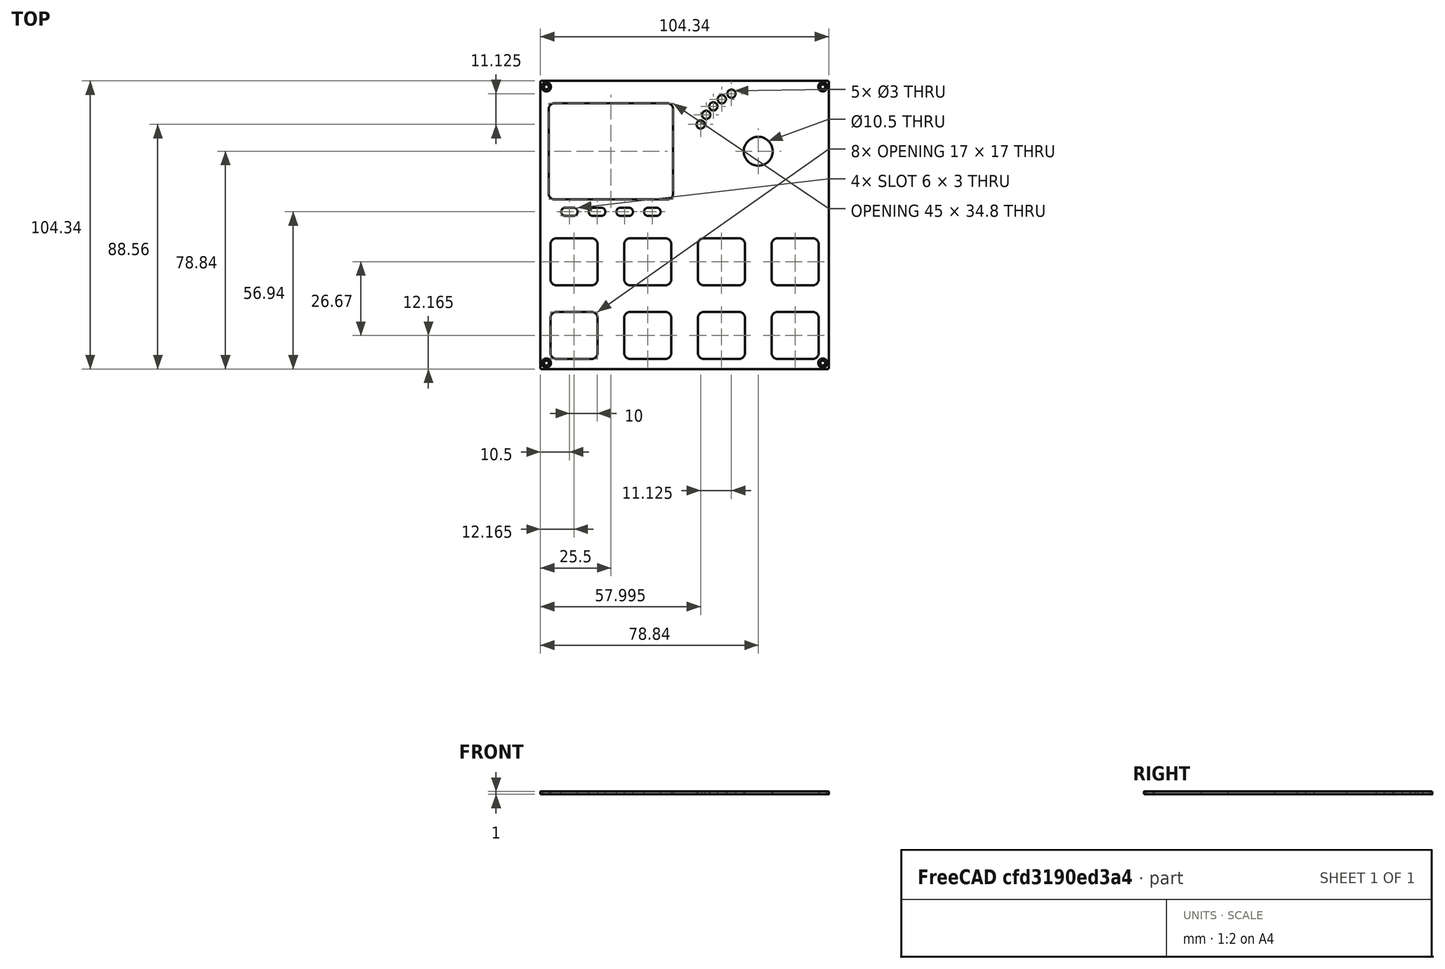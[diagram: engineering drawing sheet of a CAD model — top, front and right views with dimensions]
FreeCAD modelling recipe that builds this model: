
FCSTD DOCUMENT  (FreeCAD 0.21R33771 (Git))
Label: FRONTPANEL-SHEET-VSN1
License: All rights reserved
LicenseURL: https://en.wikipedia.org/wiki/All_rights_reserved
objects: TechDraw::DrawViewDimension×16, TechDraw::DrawViewBalloon×13, Sketcher::SketchObject×11, PartDesign::Pocket×5, TechDraw::DrawViewPart×5, TechDraw::DrawHatch×5, TechDraw::DrawViewAnnotation×4, PartDesign::Body×2, TechDraw::DrawSVGTemplate×2, TechDraw::DrawPage×2, Spreadsheet::Sheet×1, PartDesign::Pad×1, PartDesign::Hole×1, PartDesign::FeatureBase×1, TechDraw::DrawComplexSection×1
note: 54 computed .brp shape members not serialized (recipe doc carries the construction recipe); baked Part::Feature solids carry a one-line shape summary decoded from their .brp

FEATURE [Spreadsheet::Sheet] Spreadsheet  label="dim"
  cells = A1='panel_length; B1(panel_length)=104.35; A2='panel_thickness; B2(panel_thickness)=1; A3='panel_radius; B3(panel_radius)==(104.35 - 103.6) / 2; A5='corner_drill_dist; B5(corner_drill_dist)=100; A6='corner_drill_dia; B6(corner_drill_dia)=1.75; A7='corner_drill_countersink; B7(corner_drill_countersink)=3.3; A9='undercut_width; B9(undercut_width)=1; A10='undercut_length; B10(undercut_length)=90; A11='undercut_offset; B11(undercut_offset)=1; A12='undercut_depth; B12(undercut_depth)=0.8; A14='ui_raster; B14(ui_raster)=26.67; A16='light_drill_dia; B16(light_drill_dia)=3; D16='old 2.9; A17='light_bore_dia; B17(light_bore_dia)=3.45; C17='check; D17='old 3.30; E17='DEPRICATED; A18='light_bore_depth; B18(light_bore_depth)=0.4; C18='check; D18='old 0.40; E18='DEPRICATED; A20='pot_drill_dia; B20(pot_drill_dia)=9.8; C20='check; D20='old 6.20; A21='pot_led_dist; B21(pot_led_dist)=8.5; B22=0; A23='but_drill_dia; B23(but_drill_dia)=9.8; A24='but_led_dist; B24(but_led_dist)=8.5; A26='fad_cutout_width; B26(fad_cutout_width)=2.1; C26='check; D26='old 1.50; A27='fad_cutout_length; B27(fad_cutout_length)=36; A28='fad_led_dist; B28(fad_led_dist)=25; A30='enc_drill_dia; B30(enc_drill_dia)=9.8; C30='check; D30='old 6.20; A31='enc_led_dist; B31(enc_led_dist)=8.5; A33='longfad_cutout_width; B33(longfad_cutout_width)=2.1; A34='longfad_cutout_length; B34(longfad_cutout_length)=66; A36='panel_chamfer; B36(panel_chamfer)=0.2; C36='UPDATE DRAWING
FEATURE [Sketcher::SketchObject] Sketch025
  FullyConstrained = true
  MapMode = 5
  Support = -> [XY_Plane011]
  expr: Constraints[49] = <<dim>>.light_drill_dia
  sketch-geometry (28):
    g0: Circle CenterX=-26.67 CenterY=26.67 CenterZ=0 NormalX=0 NormalY=0 NormalZ=1 AngleXU=0 Radius=5.25
    g1: Circle CenterX=26.67 CenterY=26.67 CenterZ=0 NormalX=0 NormalY=0 NormalZ=1 AngleXU=0 Radius=5.25
    g2: LineSegment StartX=-26.67 StartY=26.67 StartZ=0 EndX=0 EndY=26.67 EndZ=0
    g3: LineSegment StartX=0 StartY=26.67 StartZ=0 EndX=0 EndY=0 EndZ=0
    g4: LineSegment StartX=26.67 StartY=26.67 StartZ=0 EndX=0 EndY=26.67 EndZ=0
    g5: Circle CenterX=-26.67 CenterY=26.67 CenterZ=0 NormalX=0 NormalY=0 NormalZ=1 AngleXU=0 Radius=23
    g6: Circle CenterX=26.67 CenterY=26.67 CenterZ=0 NormalX=0 NormalY=0 NormalZ=1 AngleXU=0 Radius=23
    g7: Circle CenterX=-47.5151 CenterY=36.3902 CenterZ=0 NormalX=0 NormalY=0 NormalZ=1 AngleXU=0 Radius=1.5
    g8: Circle CenterX=-45.5105 CenterY=39.8623 CenterZ=0 NormalX=0 NormalY=0 NormalZ=1 AngleXU=0 Radius=1.5
    g9: Circle CenterX=-42.9335 CenterY=42.9335 CenterZ=0 NormalX=0 NormalY=0 NormalZ=1 AngleXU=0 Radius=1.5
    g10: Circle CenterX=-39.8623 CenterY=45.5105 CenterZ=0 NormalX=0 NormalY=0 NormalZ=1 AngleXU=0 Radius=1.5
    g11: Circle CenterX=-36.3902 CenterY=47.5151 CenterZ=0 NormalX=0 NormalY=0 NormalZ=1 AngleXU=0 Radius=1.5
    g12: Circle CenterX=5.82492 CenterY=36.3902 CenterZ=0 NormalX=0 NormalY=0 NormalZ=1 AngleXU=0 Radius=1.5
    g13: Circle CenterX=7.8295 CenterY=39.8623 CenterZ=0 NormalX=0 NormalY=0 NormalZ=1 AngleXU=0 Radius=1.5
    g14: Circle CenterX=10.4065 CenterY=42.9335 CenterZ=0 NormalX=0 NormalY=0 NormalZ=1 AngleXU=0 Radius=1.5
    g15: Circle CenterX=13.4777 CenterY=45.5105 CenterZ=0 NormalX=0 NormalY=0 NormalZ=1 AngleXU=0 Radius=1.5
    g16: Circle CenterX=16.9498 CenterY=47.5151 CenterZ=0 NormalX=0 NormalY=0 NormalZ=1 AngleXU=0 Radius=1.5
    g17: LineSegment StartX=-47.5151 StartY=36.3902 StartZ=0 EndX=5.82492 EndY=36.3902 EndZ=0
    g18: LineSegment StartX=-45.5105 StartY=39.8623 StartZ=0 EndX=7.8295 EndY=39.8623 EndZ=0
    g19: LineSegment StartX=-42.9335 StartY=42.9335 StartZ=0 EndX=10.4065 EndY=42.9335 EndZ=0
    g20: LineSegment StartX=-39.8623 StartY=45.5105 StartZ=0 EndX=13.4777 EndY=45.5105 EndZ=0
    g21: LineSegment StartX=-36.3902 StartY=47.5151 StartZ=0 EndX=16.9498 EndY=47.5151 EndZ=0
    g22: LineSegment StartX=5.82492 StartY=36.3902 StartZ=0 EndX=26.67 EndY=26.67 EndZ=0
    g23: LineSegment StartX=16.9498 StartY=47.5151 StartZ=0 EndX=26.67 EndY=26.67 EndZ=0
    g24: LineSegment StartX=5.82492 StartY=36.3902 StartZ=0 EndX=7.8295 EndY=39.8623 EndZ=0
    g25: LineSegment StartX=7.8295 StartY=39.8623 StartZ=0 EndX=10.4065 EndY=42.9335 EndZ=0
    g26: LineSegment StartX=13.4777 StartY=45.5105 StartZ=0 EndX=10.4065 EndY=42.9335 EndZ=0
    g27: LineSegment StartX=16.9498 StartY=47.5151 StartZ=0 EndX=13.4777 EndY=45.5105 EndZ=0
  constraints (69):
    c: Coincident(g2,g0)
    c: PointOnObject(g2,g-2)
    c: Coincident(g2,g3)
    c: Coincident(g3,g-1)
    c: Coincident(g4,g1)
    c: Coincident(g4,g2)
    c: Equal(g3,g2)
    c: Equal(g2,g4)
    c: Horizontal(g2)
    c: Horizontal(g4)
    c: DistanceY(g3,g3) = 26.67
    c: Equal(g0,g1)
    c: Coincident(g5,g0)
    c: Coincident(g6,g1)
    c: Equal(g6,g5)
    c: PointOnObject(g7,g5)
    c: PointOnObject(g8,g5)
    c: PointOnObject(g9,g5)
    c: PointOnObject(g10,g5)
    c: PointOnObject(g11,g5)
    c: PointOnObject(g12,g6)
    c: PointOnObject(g13,g6)
    c: PointOnObject(g14,g6)
    c: PointOnObject(g15,g6)
    c: PointOnObject(g16,g6)
    c: Equal(g7,g8)
    c: Equal(g8,g9)
    c: Equal(g9,g10)
    c: Equal(g10,g11)
    c: Equal(g11,g12)
    c: Equal(g12,g13)
    c: Equal(g13,g14)
    c: Equal(g14,g15)
    c: Equal(g15,g16)
    c: Coincident(g17,g7)
    c: Coincident(g17,g12)
    c: Coincident(g18,g8)
    c: Coincident(g18,g13)
    c: Horizontal(g18)
    c: Coincident(g19,g9)
    c: Coincident(g19,g14)
    c: Horizontal(g19)
    c: Coincident(g20,g10)
    c: Coincident(g20,g15)
    c: Horizontal(g20)
    c: Coincident(g21,g11)
    c: Horizontal(g21)
    c: Coincident(g21,g16)
    c: Horizontal(g17)
    c: Diameter(g12) = 3
    c: Coincident(g22,g12)
    c: Coincident(g22,g1)
    c: Coincident(g23,g16)
    c: Coincident(g23,g1)
    c: Angle(g22,g4) = 0.436332
    c: Angle(g-2,g23) = 0.436332
    c: Coincident(g24,g12)
    c: Coincident(g24,g13)
    c: Coincident(g25,g13)
    c: Coincident(g26,g15)
    c: Coincident(g26,g25)
    c: Coincident(g27,g16)
    c: Coincident(g27,g15)
    c: Coincident(g25,g14)
    c: Equal(g24,g25)
    c: Equal(g25,g26)
    c: Equal(g26,g27)
    c: Radius(g6) = 23
    c: Diameter(g1) = 10.5
FEATURE [Sketcher::SketchObject] Sketch024  label="TEK2_ButtonLight"
  FullyConstrained = true
  MapMode = 5
  Support = -> [XY_Plane011]
  expr: Constraints[42] = <<dim>>.but_led_dist
  sketch-geometry (17):
    g0: Circle CenterX=-40.005 CenterY=-4.835 CenterZ=0 NormalX=0 NormalY=0 NormalZ=1 AngleXU=0 Radius=2
    g1: Circle CenterX=-13.335 CenterY=-4.835 CenterZ=0 NormalX=0 NormalY=0 NormalZ=1 AngleXU=0 Radius=2
    g2: LineSegment StartX=-40.005 StartY=-4.835 StartZ=0 EndX=-13.335 EndY=-4.835 EndZ=0
    g3: Circle CenterX=13.335 CenterY=-4.835 CenterZ=0 NormalX=0 NormalY=0 NormalZ=1 AngleXU=0 Radius=2
    g4: LineSegment StartX=-13.335 StartY=-4.835 StartZ=0 EndX=13.335 EndY=-4.835 EndZ=0
    g5: Circle CenterX=40.005 CenterY=-4.835 CenterZ=0 NormalX=0 NormalY=0 NormalZ=1 AngleXU=0 Radius=2
    g6: LineSegment StartX=13.335 StartY=-4.835 StartZ=0 EndX=40.005 EndY=-4.835 EndZ=0
    g7: Circle CenterX=-40.005 CenterY=-31.505 CenterZ=0 NormalX=0 NormalY=0 NormalZ=1 AngleXU=0 Radius=2
    g8: LineSegment StartX=-40.005 StartY=-4.835 StartZ=0 EndX=-40.005 EndY=-31.505 EndZ=0
    g9: Circle CenterX=-13.335 CenterY=-31.505 CenterZ=0 NormalX=0 NormalY=0 NormalZ=1 AngleXU=0 Radius=2
    g10: LineSegment StartX=-40.005 StartY=-31.505 StartZ=0 EndX=-13.335 EndY=-31.505 EndZ=0
    g11: Circle CenterX=13.335 CenterY=-31.505 CenterZ=0 NormalX=0 NormalY=0 NormalZ=1 AngleXU=0 Radius=2
    g12: LineSegment StartX=-13.335 StartY=-31.505 StartZ=0 EndX=13.335 EndY=-31.505 EndZ=0
    g13: Circle CenterX=40.005 CenterY=-31.505 CenterZ=0 NormalX=0 NormalY=0 NormalZ=1 AngleXU=0 Radius=2
    g14: LineSegment StartX=13.335 StartY=-31.505 StartZ=0 EndX=40.005 EndY=-31.505 EndZ=0
    g15: LineSegment StartX=-13.335 StartY=-4.835 StartZ=0 EndX=-1.8e-15 EndY=8.5 EndZ=0
    g16: LineSegment StartX=-1.8e-15 StartY=8.5 StartZ=0 EndX=13.335 EndY=-4.835 EndZ=0
  constraints (43):
    c: Diameter(g0) = 4
    c: Coincident(g0,g2)
    c: Coincident(g1,g2)
    c: Coincident(g1,g4)
    c: Coincident(g3,g4)
    c: Coincident(g3,g6)
    c: Coincident(g5,g6)
    c: Coincident(g0,g8)
    c: Coincident(g7,g8)
    c: Coincident(g7,g10)
    c: Coincident(g9,g10)
    c: Coincident(g9,g12)
    c: Coincident(g11,g12)
    c: Coincident(g11,g14)
    c: Coincident(g13,g14)
    c: Horizontal(g4)
    c: Horizontal(g2)
    c: Horizontal(g6)
    c: Horizontal(g10)
    c: Horizontal(g12)
    c: Horizontal(g14)
    c: Vertical(g8)
    c: Equal(g8,g2)
    c: Equal(g2,g10)
    c: Equal(g10,g12)
    c: Equal(g12,g4)
    c: Equal(g4,g6)
    c: Equal(g6,g14)
    c: DistanceX(g4,g4) = 26.67
    c: Equal(g7,g9)
    c: Equal(g9,g11)
    c: Equal(g11,g13)
    c: Equal(g13,g5)
    c: Equal(g5,g3)
    c: Equal(g3,g1)
    c: Equal(g1,g0)
    c: Coincident(g15,g1)
    c: PointOnObject(g15,g-2)
    c: Coincident(g15,g16)
    c: Coincident(g16,g3)
    c: Equal(g16,g15)
    c: Perpendicular(g15,g16)
    c: DistanceY(g-1,g15) = 8.5
FEATURE [Sketcher::SketchObject] Sketch023  label="TEK2_ButtonHole"
  FullyConstrained = true
  MapMode = 5
  Support = -> [XY_Plane011]
  sketch-geometry (17):
    g0: Circle CenterX=-40.005 CenterY=-13.335 CenterZ=0 NormalX=0 NormalY=0 NormalZ=1 AngleXU=0 Radius=2
    g1: Circle CenterX=-13.335 CenterY=-13.335 CenterZ=0 NormalX=0 NormalY=0 NormalZ=1 AngleXU=0 Radius=2
    g2: LineSegment StartX=-40.005 StartY=-13.335 StartZ=0 EndX=-13.335 EndY=-13.335 EndZ=0
    g3: Circle CenterX=13.335 CenterY=-13.335 CenterZ=0 NormalX=0 NormalY=0 NormalZ=1 AngleXU=0 Radius=2
    g4: LineSegment StartX=-13.335 StartY=-13.335 StartZ=0 EndX=13.335 EndY=-13.335 EndZ=0
    g5: Circle CenterX=40.005 CenterY=-13.335 CenterZ=0 NormalX=0 NormalY=0 NormalZ=1 AngleXU=0 Radius=2
    g6: LineSegment StartX=13.335 StartY=-13.335 StartZ=0 EndX=40.005 EndY=-13.335 EndZ=0
    g7: Circle CenterX=-40.005 CenterY=-40.005 CenterZ=0 NormalX=0 NormalY=0 NormalZ=1 AngleXU=0 Radius=2
    g8: LineSegment StartX=-40.005 StartY=-13.335 StartZ=0 EndX=-40.005 EndY=-40.005 EndZ=0
    g9: Circle CenterX=-13.335 CenterY=-40.005 CenterZ=0 NormalX=0 NormalY=0 NormalZ=1 AngleXU=0 Radius=2
    g10: LineSegment StartX=-40.005 StartY=-40.005 StartZ=0 EndX=-13.335 EndY=-40.005 EndZ=0
    g11: Circle CenterX=13.335 CenterY=-40.005 CenterZ=0 NormalX=0 NormalY=0 NormalZ=1 AngleXU=0 Radius=2
    g12: LineSegment StartX=-13.335 StartY=-40.005 StartZ=0 EndX=13.335 EndY=-40.005 EndZ=0
    g13: Circle CenterX=40.005 CenterY=-40.005 CenterZ=0 NormalX=0 NormalY=0 NormalZ=1 AngleXU=0 Radius=2
    g14: LineSegment StartX=13.335 StartY=-40.005 StartZ=0 EndX=40.005 EndY=-40.005 EndZ=0
    g15: LineSegment StartX=0 StartY=0 StartZ=0 EndX=13.335 EndY=-13.335 EndZ=0
    g16: LineSegment StartX=0 StartY=0 StartZ=0 EndX=-13.335 EndY=-13.335 EndZ=0
  constraints (42):
    c: Diameter(g0) = 4
    c: Coincident(g0,g2)
    c: Coincident(g1,g2)
    c: Coincident(g1,g4)
    c: Coincident(g3,g4)
    c: Coincident(g3,g6)
    c: Coincident(g5,g6)
    c: Coincident(g0,g8)
    c: Coincident(g7,g8)
    c: Coincident(g7,g10)
    c: Coincident(g9,g10)
    c: Coincident(g9,g12)
    c: Coincident(g11,g12)
    c: Coincident(g11,g14)
    c: Coincident(g13,g14)
    c: Coincident(g-1,g16)
    c: Coincident(g16,g1)
    c: Coincident(g15,g3)
    c: Horizontal(g4)
    c: Horizontal(g2)
    c: Horizontal(g6)
    c: Horizontal(g10)
    c: Horizontal(g12)
    c: Horizontal(g14)
    c: Vertical(g8)
    c: Equal(g8,g2)
    c: Equal(g2,g10)
    c: Equal(g10,g12)
    c: Equal(g12,g4)
    c: Equal(g4,g6)
    c: Equal(g6,g14)
    c: DistanceX(g4,g4) = 26.67
    c: Equal(g16,g15)
    c: Coincident(g15,g16)
    c: Perpendicular(g15,g16)
    c: Equal(g7,g9)
    c: Equal(g9,g11)
    c: Equal(g11,g13)
    c: Equal(g13,g5)
    c: Equal(g5,g3)
    c: Equal(g3,g1)
    c: Equal(g1,g0)
FEATURE [Sketcher::SketchObject] Sketch001
  FullyConstrained = true
  MapMode = 5
  Support = -> [XY_Plane]
  expr: Constraints[13] = <<dim>>.corner_drill_dist
  sketch-geometry (9):
    g0: LineSegment StartX=-50 StartY=50 StartZ=0 EndX=-50 EndY=-50 EndZ=0
    g1: LineSegment StartX=-50 StartY=-50 StartZ=0 EndX=50 EndY=-50 EndZ=0
    g2: LineSegment StartX=50 StartY=-50 StartZ=0 EndX=50 EndY=50 EndZ=0
    g3: LineSegment StartX=50 StartY=50 StartZ=0 EndX=-50 EndY=50 EndZ=0
    g4: Circle CenterX=0 CenterY=0 CenterZ=0 NormalX=0 NormalY=0 NormalZ=1 AngleXU=0 Radius=70.7107
    g5: Circle CenterX=-50 CenterY=50 CenterZ=0 NormalX=0 NormalY=0 NormalZ=1 AngleXU=0 Radius=0.5
    g6: Circle CenterX=50 CenterY=50 CenterZ=0 NormalX=0 NormalY=0 NormalZ=1 AngleXU=0 Radius=0.5
    g7: Circle CenterX=50 CenterY=-50 CenterZ=0 NormalX=0 NormalY=0 NormalZ=1 AngleXU=0 Radius=0.5
    g8: Circle CenterX=-50 CenterY=-50 CenterZ=0 NormalX=0 NormalY=0 NormalZ=1 AngleXU=0 Radius=0.5
  constraints (22):
    c: Coincident(g0,g1)
    c: Coincident(g1,g2)
    c: Coincident(g2,g3)
    c: Coincident(g3,g0)
    c: Equal(g0,g1)
    c: Equal(g0,g2)
    c: Equal(g0,g3)
    c: PointOnObject(g0,g4)
    c: PointOnObject(g1,g4)
    c: PointOnObject(g2,g4)
    c: PointOnObject(g3,g4)
    c: Coincident(g4,g-1)
    c: Horizontal(g3)
    c: DistanceX(g3,g3) = 100
    c: Coincident(g5,g0)
    c: Coincident(g6,g2)
    c: Coincident(g7,g1)
    c: Coincident(g8,g0)
    c: Diameter(g8) = 1
    c: Equal(g8,g7)
    c: Equal(g8,g6)
    c: Equal(g8,g5)
FEATURE [Sketcher::SketchObject] Sketch002
  AttachmentOffset = pos=(0,0,-4.8) rot=(0,0,1;0rad)
  FullyConstrained = true
  MapMode = 5
  Placement = pos=(0,0,-4.8) rot=(0,0,1;0rad)
  Support = -> [XY_Plane]
  expr: .AttachmentOffset.Base.z = -<<dim>>.undercut_depth - 4
  expr: Constraints[91] = <<dim>>.undercut_length
  expr: Constraints[92] = <<dim>>.undercut_width
  expr: Constraints[93] = <<dim>>.panel_length / 2 - <<dim>>.undercut_offset - <<dim>>.undercut_width / 2
  sketch-geometry (40):
    g0: LineSegment StartX=-45 StartY=50.175 StartZ=0 EndX=45 EndY=50.175 EndZ=0
    g1: LineSegment StartX=-45 StartY=51.175 StartZ=0 EndX=45 EndY=51.175 EndZ=0
    g2: LineSegment StartX=-50.675 StartY=45 StartZ=0 EndX=0 EndY=0 EndZ=0
    g3: LineSegment StartX=0 StartY=0 StartZ=0 EndX=-50.675 EndY=-45 EndZ=0
    g4: LineSegment StartX=0 StartY=0 StartZ=0 EndX=-45 EndY=50.675 EndZ=0
    g5: LineSegment StartX=45 StartY=50.675 StartZ=0 EndX=0 EndY=0 EndZ=0
    g6: LineSegment StartX=0 StartY=0 StartZ=0 EndX=50.675 EndY=45 EndZ=0
    g7: LineSegment StartX=50.675 StartY=-45 StartZ=0 EndX=0 EndY=0 EndZ=0
    g8: LineSegment StartX=0 StartY=0 StartZ=0 EndX=45 EndY=-50.675 EndZ=0
    g9: LineSegment StartX=0 StartY=0 StartZ=0 EndX=-45 EndY=-50.675 EndZ=0
    g10: ArcOfCircle CenterX=45 CenterY=50.675 CenterZ=0 NormalX=0 NormalY=0 NormalZ=1 AngleXU=0 Radius=0.5 StartAngle=4.71239 EndAngle=6.28319
    g11: ArcOfCircle CenterX=45 CenterY=50.675 CenterZ=0 NormalX=0 NormalY=0 NormalZ=1 AngleXU=0 Radius=0.5 StartAngle=0 EndAngle=1.5708
    g12: LineSegment StartX=45 StartY=50.675 StartZ=0 EndX=45.5 EndY=50.675 EndZ=0
    g13: ArcOfCircle CenterX=-45 CenterY=50.675 CenterZ=0 NormalX=0 NormalY=0 NormalZ=1 AngleXU=0 Radius=0.5 StartAngle=3.14159 EndAngle=4.71239
    g14: ArcOfCircle CenterX=-45 CenterY=50.675 CenterZ=0 NormalX=0 NormalY=0 NormalZ=1 AngleXU=0 Radius=0.5 StartAngle=1.5708 EndAngle=3.14159
    g15: LineSegment StartX=-45.5 StartY=50.675 StartZ=0 EndX=-45 EndY=50.675 EndZ=0
    g16: LineSegment StartX=-45 StartY=-51.175 StartZ=0 EndX=45 EndY=-51.175 EndZ=0
    g17: LineSegment StartX=-45 StartY=-50.175 StartZ=0 EndX=45 EndY=-50.175 EndZ=0
    g18: ArcOfCircle CenterX=45 CenterY=-50.675 CenterZ=0 NormalX=0 NormalY=0 NormalZ=1 AngleXU=0 Radius=0.5 StartAngle=4.71239 EndAngle=6.28319
    g19: ArcOfCircle CenterX=45 CenterY=-50.675 CenterZ=0 NormalX=0 NormalY=0 NormalZ=1 AngleXU=0 Radius=0.5 StartAngle=0 EndAngle=1.5708
    g20: LineSegment StartX=45 StartY=-50.675 StartZ=0 EndX=45.5 EndY=-50.675 EndZ=0
    g21: ArcOfCircle CenterX=-45 CenterY=-50.675 CenterZ=0 NormalX=0 NormalY=0 NormalZ=1 AngleXU=0 Radius=0.5 StartAngle=3.14159 EndAngle=4.71239
    g22: ArcOfCircle CenterX=-45 CenterY=-50.675 CenterZ=0 NormalX=0 NormalY=0 NormalZ=1 AngleXU=0 Radius=0.5 StartAngle=1.5708 EndAngle=3.14159
    g23: LineSegment StartX=-45.5 StartY=-50.675 StartZ=0 EndX=-45 EndY=-50.675 EndZ=0
    g24: LineSegment StartX=51.175 StartY=-45 StartZ=0 EndX=51.175 EndY=45 EndZ=0
    g25: LineSegment StartX=50.175 StartY=-45 StartZ=0 EndX=50.175 EndY=45 EndZ=0
    g26: ArcOfCircle CenterX=50.675 CenterY=45 CenterZ=0 NormalX=0 NormalY=0 NormalZ=1 AngleXU=0 Radius=0.5 StartAngle=3.8e-15 EndAngle=1.5708
    g27: ArcOfCircle CenterX=50.675 CenterY=45 CenterZ=0 NormalX=0 NormalY=0 NormalZ=1 AngleXU=0 Radius=0.5 StartAngle=1.5708 EndAngle=3.14159
    g28: LineSegment StartX=50.675 StartY=45 StartZ=0 EndX=50.675 EndY=45.5 EndZ=0
    g29: ArcOfCircle CenterX=50.675 CenterY=-45 CenterZ=0 NormalX=0 NormalY=0 NormalZ=1 AngleXU=0 Radius=0.5 StartAngle=4.71239 EndAngle=6.28319
    g30: ArcOfCircle CenterX=50.675 CenterY=-45 CenterZ=0 NormalX=0 NormalY=0 NormalZ=1 AngleXU=0 Radius=0.5 StartAngle=3.14159 EndAngle=4.71239
    g31: LineSegment StartX=50.675 StartY=-45.5 StartZ=0 EndX=50.675 EndY=-45 EndZ=0
    g32: LineSegment StartX=-50.175 StartY=-45 StartZ=0 EndX=-50.175 EndY=45 EndZ=0
    g33: LineSegment StartX=-51.175 StartY=-45 StartZ=0 EndX=-51.175 EndY=45 EndZ=0
    g34: ArcOfCircle CenterX=-50.675 CenterY=45 CenterZ=0 NormalX=0 NormalY=0 NormalZ=1 AngleXU=0 Radius=0.5 StartAngle=1.4e-15 EndAngle=1.5708
    g35: ArcOfCircle CenterX=-50.675 CenterY=45 CenterZ=0 NormalX=0 NormalY=0 NormalZ=1 AngleXU=0 Radius=0.5 StartAngle=1.5708 EndAngle=3.14159
    g36: LineSegment StartX=-50.675 StartY=45 StartZ=0 EndX=-50.675 EndY=45.5 EndZ=0
    g37: ArcOfCircle CenterX=-50.675 CenterY=-45 CenterZ=0 NormalX=0 NormalY=0 NormalZ=1 AngleXU=0 Radius=0.5 StartAngle=4.71239 EndAngle=6.28319
    g38: ArcOfCircle CenterX=-50.675 CenterY=-45 CenterZ=0 NormalX=0 NormalY=0 NormalZ=1 AngleXU=0 Radius=0.5 StartAngle=3.14159 EndAngle=4.71239
    g39: LineSegment StartX=-50.675 StartY=-45.5 StartZ=0 EndX=-50.675 EndY=-45 EndZ=0
  constraints (96):
    c: Horizontal(g0)
    c: Coincident(g2,g-1)
    c: Coincident(g2,g3)
    c: Coincident(g-1,g4)
    c: Coincident(g5,g-1)
    c: Coincident(g5,g6)
    c: Coincident(g7,g-1)
    c: Coincident(g7,g8)
    c: Coincident(g-1,g9)
    c: Equal(g5,g6)
    c: Equal(g6,g8)
    c: Equal(g8,g7)
    c: Equal(g7,g9)
    c: Equal(g9,g3)
    c: Equal(g3,g2)
    c: Equal(g2,g4)
    c: Coincident(g10,g5)
    c: Coincident(g11,g10)
    c: Coincident(g11,g10)
    c: Tangent(g11,g1) = 1.5708
    c: Tangent(g10,g0) = -1.5708
    c: Coincident(g12,g10)
    c: Coincident(g12,g10)
    c: Horizontal(g12)
    c: Coincident(g13,g4)
    c: Coincident(g14,g13)
    c: Coincident(g14,g13)
    c: Tangent(g14,g1) = 1.5708
    c: Tangent(g13,g0) = -1.5708
    c: Coincident(g15,g13)
    c: Coincident(g15,g13)
    c: Horizontal(g15)
    c: Horizontal(g1)
    c: Horizontal(g16)
    c: Coincident(g19,g18)
    c: Coincident(g19,g18)
    c: Tangent(g19,g17) = 1.5708
    c: Tangent(g18,g16) = -1.5708
    c: Coincident(g20,g18)
    c: Coincident(g20,g18)
    c: Horizontal(g20)
    c: Coincident(g22,g21)
    c: Coincident(g22,g21)
    c: Tangent(g22,g17) = 1.5708
    c: Tangent(g21,g16) = -1.5708
    c: Coincident(g23,g21)
    c: Coincident(g23,g21)
    c: Horizontal(g23)
    c: Horizontal(g17)
    c: Coincident(g21,g9)
    c: Coincident(g8,g18)
    c: Equal(g22,g14)
    c: Equal(g17,g1)
    c: Coincident(g27,g26)
    c: Coincident(g27,g26)
    c: Tangent(g27,g25) = 1.5708
    c: Tangent(g26,g24) = -1.5708
    c: Coincident(g28,g26)
    c: Coincident(g28,g26)
    c: Coincident(g30,g29)
    c: Coincident(g30,g29)
    c: Tangent(g30,g25) = 1.5708
    c: Tangent(g29,g24) = -1.5708
    c: Coincident(g31,g29)
    c: Coincident(g31,g29)
    c: Vertical(g31)
    c: Vertical(g28)
    c: Vertical(g25)
    c: Vertical(g24)
    c: Coincident(g35,g34)
    c: Coincident(g35,g34)
    c: Tangent(g35,g33) = 1.5708
    c: Tangent(g34,g32) = -1.5708
    c: Coincident(g36,g34)
    c: Coincident(g36,g34)
    c: Coincident(g38,g37)
    c: Coincident(g38,g37)
    c: Tangent(g38,g33) = 1.5708
    c: Tangent(g37,g32) = -1.5708
    c: Coincident(g39,g37)
    c: Coincident(g39,g37)
    c: Vertical(g39)
    c: Vertical(g36)
    c: Vertical(g33)
    c: Vertical(g32)
    c: Coincident(g6,g26)
    c: Coincident(g7,g29)
    c: Equal(g25,g0)
    c: Equal(g11,g27)
    c: Equal(g1,g33)
    c: Equal(g35,g11)
    c: DistanceX(g13,g10) = 90
    c: Diameter(g13) = 1
    c: DistanceY(g-1,g13) = 50.675
    c: Coincident(g2,g34)
    c: Coincident(g3,g37)
FEATURE [Sketcher::SketchObject] Sketch
  FullyConstrained = true
  MapMode = 5
  Support = -> [XY_Plane]
  expr: Constraints[12] = <<dim>>.panel_radius
  expr: Constraints[16] = <<dim>>.panel_length
  sketch-geometry (11):
    g0: LineSegment StartX=-51.8 StartY=52.175 StartZ=0 EndX=51.8 EndY=52.175 EndZ=0
    g1: LineSegment StartX=52.175 StartY=51.8 StartZ=0 EndX=52.175 EndY=-51.8 EndZ=0
    g2: LineSegment StartX=51.8 StartY=-52.175 StartZ=0 EndX=-51.8 EndY=-52.175 EndZ=0
    g3: LineSegment StartX=-52.175 StartY=-51.8 StartZ=0 EndX=-52.175 EndY=51.8 EndZ=0
    g4: ArcOfCircle CenterX=-51.8 CenterY=51.8 CenterZ=0 NormalX=0 NormalY=0 NormalZ=1 AngleXU=0 Radius=0.375 StartAngle=1.5708 EndAngle=3.14159
    g5: ArcOfCircle CenterX=51.8 CenterY=51.8 CenterZ=0 NormalX=0 NormalY=0 NormalZ=1 AngleXU=0 Radius=0.375 StartAngle=8.4e-15 EndAngle=1.5708
    g6: ArcOfCircle CenterX=51.8 CenterY=-51.8 CenterZ=0 NormalX=0 NormalY=0 NormalZ=1 AngleXU=0 Radius=0.375 StartAngle=4.71239 EndAngle=6.28319
    g7: ArcOfCircle CenterX=-51.8 CenterY=-51.8 CenterZ=0 NormalX=0 NormalY=0 NormalZ=1 AngleXU=0 Radius=0.375 StartAngle=3.14159 EndAngle=4.71239
    g8: LineSegment StartX=-51.8 StartY=51.8 StartZ=0 EndX=0 EndY=0 EndZ=0
    g9: LineSegment StartX=0 StartY=0 StartZ=0 EndX=51.8 EndY=51.8 EndZ=0
    g10: LineSegment StartX=0 StartY=0 StartZ=0 EndX=-51.8 EndY=-51.8 EndZ=0
  constraints (26):
    c: Horizontal(g0)
    c: Horizontal(g2)
    c: Vertical(g1)
    c: Vertical(g3)
    c: Tangent(g3,g4) = 1.5708
    c: Tangent(g0,g4) = 1.5708
    c: Tangent(g0,g5) = 1.5708
    c: Tangent(g1,g5) = 1.5708
    c: Tangent(g1,g6) = 1.5708
    c: Tangent(g2,g6) = 1.5708
    c: Tangent(g2,g7) = 1.5708
    c: Tangent(g3,g7) = 1.5708
    c: Radius(g4) = 0.375
    c: Equal(g4,g5)
    c: Equal(g4,g6)
    c: Equal(g4,g7)
    c: DistanceX(g3,g1) = 104.35
    c: Equal(g3,g0)
    c: Coincident(g8,g4)
    c: Coincident(g8,g-1)
    c: Coincident(g8,g9)
    c: Coincident(g9,g5)
    c: Coincident(g-1,g10)
    c: Coincident(g10,g7)
    c: Equal(g10,g8)
    c: Equal(g8,g9)
FEATURE [PartDesign::Pad] Pad  label="panel"
  AllowMultiFace = false
  Direction = (0,0,1)
  Length = 1
  Length2 = 100
  Profile = -> Sketch
  Reversed = true
  Type = 0
  expr: Length = <<dim>>.panel_thickness
FEATURE [PartDesign::Pocket] Pocket
  AllowMultiFace = false
  BaseFeature = -> Pad
  Direction = (0,0,-1)
  Length = 5
  Length2 = 100
  Profile = -> Sketch002
  Type = 1
FEATURE [PartDesign::Hole] Hole
  BaseFeature = -> Pocket
  CustomThreadClearance = 0
  Depth = 298.105
  DepthType = 1
  Diameter = 1.75
  DrillForDepth = false
  DrillPoint = 1
  DrillPointAngle = 118
  HoleCutCountersinkAngle = 90
  HoleCutCustomValues = false
  HoleCutDepth = 0
  HoleCutDiameter = 3.3
  HoleCutType = 2
  ModelThread = false
  Profile = -> Sketch001
  Tapered = false
  TaperedAngle = 90
  ThreadClass = 0
  ThreadDepth = 298.105
  ThreadDepthType = 0
  ThreadDirection = 0
  ThreadFit = 0
  ThreadSize = 0
  ThreadType = 0
  Threaded = false
  UseCustomThreadClearance = false
  expr: Diameter = <<dim>>.corner_drill_dia
  expr: HoleCutDiameter = <<dim>>.corner_drill_countersink
FEATURE [PartDesign::Body] Body  label="Base"
  Group = -> [Sketch,Pad,Sketch001,Sketch002,Pocket,Hole]
  Origin = -> Origin
  Tip = -> Hole
FEATURE [PartDesign::FeatureBase] Clone009
  BaseFeature = -> Body
FEATURE [PartDesign::Pocket] Pocket007  label="TEK2_TEK_Light"
  BaseFeature = -> Clone009
  Direction = (0,0,-1)
  Length = 5
  Length2 = 5
  Profile = -> Sketch025
  ReferenceAxis = -> Sketch025 [N_Axis]
  Type = 0
FEATURE [Sketcher::SketchObject] Sketch026  label="Section A-A"
  FullyConstrained = true
  MapMode = 5
  Support = -> [XY_Plane011]
  sketch-geometry (2):
    g0: LineSegment StartX=-53.5 StartY=-50 StartZ=0 EndX=-46.5 EndY=-50 EndZ=0
    g1: GeomPoint X=-50 Y=-50 Z=0
  constraints (5):
    c: Horizontal(g0)
    c: DistanceX(g0,g0) = 7
    c: DistanceY(g0,g-1) = 50
    c: Symmetric(g0,g0,g1)
    c: DistanceX(g1,g-1) = 50
FEATURE [Sketcher::SketchObject] Sketch027
  FullyConstrained = true
  MapMode = 5
  Support = -> [XY_Plane011]
  sketch-geometry (11):
    g0: LineSegment StartX=-49.17 StartY=11.27 StartZ=0 EndX=-49.17 EndY=42.07 EndZ=0
    g1: LineSegment StartX=-47.17 StartY=44.07 StartZ=0 EndX=-6.17 EndY=44.07 EndZ=0
    g2: LineSegment StartX=-4.17 StartY=42.07 StartZ=0 EndX=-4.17 EndY=11.27 EndZ=0
    g3: LineSegment StartX=-6.17 StartY=9.27 StartZ=0 EndX=-47.17 EndY=9.27 EndZ=0
    g4: GeomPoint X=-26.67 Y=26.67 Z=0
    g5: ArcOfCircle CenterX=-47.17 CenterY=42.07 CenterZ=0 NormalX=0 NormalY=0 NormalZ=1 AngleXU=0 Radius=2 StartAngle=1.5708 EndAngle=3.14159
    g6: ArcOfCircle CenterX=-6.17 CenterY=42.07 CenterZ=0 NormalX=0 NormalY=0 NormalZ=1 AngleXU=0 Radius=2 StartAngle=0 EndAngle=1.5708
    g7: ArcOfCircle CenterX=-6.17 CenterY=11.27 CenterZ=0 NormalX=0 NormalY=0 NormalZ=1 AngleXU=0 Radius=2 StartAngle=4.71239 EndAngle=6.28319
    g8: ArcOfCircle CenterX=-47.17 CenterY=11.27 CenterZ=0 NormalX=0 NormalY=0 NormalZ=1 AngleXU=0 Radius=2 StartAngle=3.14159 EndAngle=4.71239
    g9: LineSegment StartX=-26.67 StartY=44.07 StartZ=0 EndX=-26.67 EndY=9.27 EndZ=0
    g10: LineSegment StartX=-49.17 StartY=26.67 StartZ=0 EndX=-4.17 EndY=26.67 EndZ=0
  constraints (29):
    c: Horizontal(g1)
    c: Horizontal(g3)
    c: Vertical(g0)
    c: Vertical(g2)
    c: DistanceY(g-1,g4) = 26.67
    c: Tangent(g1,g5) = 1.5708
    c: Tangent(g0,g5) = 1.5708
    c: Tangent(g1,g6) = 1.5708
    c: Tangent(g2,g6) = 1.5708
    c: Tangent(g2,g7) = 1.5708
    c: Tangent(g3,g7) = 1.5708
    c: Tangent(g3,g8) = 1.5708
    c: Tangent(g0,g8) = 1.5708
    c: Equal(g5,g6)
    c: Equal(g6,g7)
    c: Equal(g7,g8)
    c: DistanceX(g0,g2) = 45
    c: DistanceY(g3,g1) = 34.8
    c: PointOnObject(g9,g3)
    c: Vertical(g9)
    c: PointOnObject(g10,g0)
    c: Horizontal(g10)
    c: Symmetric(g2,g2,g10)
    c: Symmetric(g1,g1,g9)
    c: PointOnObject(g4,g9)
    c: PointOnObject(g4,g10)
    c: Diameter(g6) = 4
    c: DistanceX(g4,g-1) = 26.67
    c: DistanceY(g-1,g3) = 9.27
FEATURE [PartDesign::Pocket] Pocket008  label="TEK1_display"
  BaseFeature = -> Pocket007
  Direction = (0,0,-1)
  Length = 5
  Length2 = 5
  Profile = -> Sketch027
  ReferenceAxis = -> Sketch027 [N_Axis]
  Type = 1
FEATURE [Sketcher::SketchObject] Sketch028  label="LocatorPin"
  FullyConstrained = true
  MapMode = 5
  Support = -> [XY_Plane011]
  sketch-geometry (3):
    g0: Circle CenterX=-48.77 CenterY=8.17 CenterZ=0 NormalX=0 NormalY=0 NormalZ=1 AngleXU=0 Radius=0.6
    g1: Circle CenterX=-4.57 CenterY=45.17 CenterZ=0 NormalX=0 NormalY=0 NormalZ=1 AngleXU=0 Radius=0.6
    g2: GeomPoint X=-26.67 Y=26.67 Z=0
  constraints (8):
    c: Equal(g1,g0)
    c: Diameter(g1) = 1.2
    c: DistanceX(g2,g-1) = 26.67
    c: DistanceY(g-1,g2) = 26.67
    c: DistanceX(g0,g2) = 22.1
    c: DistanceY(g0,g2) = 18.5
    c: DistanceX(g2,g1) = 22.1
    c: DistanceY(g2,g1) = 18.5
FEATURE [Sketcher::SketchObject] Sketch029
  FullyConstrained = true
  MapMode = 5
  Support = -> [XY_Plane011]
  sketch-geometry (39):
    g0: LineSegment StartX=-47.07 StartY=4.77 StartZ=0 EndX=-6.27 EndY=4.77 EndZ=0
    g1: GeomPoint X=-26.67 Y=4.77 Z=0
    g2: LineSegment StartX=-34.67 StartY=3.12 StartZ=0 EndX=-34.67 EndY=6.42 EndZ=0
    g3: LineSegment StartX=-34.67 StartY=6.42 StartZ=0 EndX=-28.67 EndY=6.42 EndZ=0
    g4: LineSegment StartX=-28.67 StartY=6.42 StartZ=0 EndX=-28.67 EndY=3.12 EndZ=0
    g5: LineSegment StartX=-28.67 StartY=3.12 StartZ=0 EndX=-34.67 EndY=3.12 EndZ=0
    g6: GeomPoint X=-31.67 Y=4.77 Z=0
    g7: LineSegment StartX=-44.67 StartY=3.12 StartZ=0 EndX=-44.67 EndY=6.42 EndZ=0
    g8: LineSegment StartX=-44.67 StartY=6.42 StartZ=0 EndX=-38.67 EndY=6.42 EndZ=0
    g9: LineSegment StartX=-38.67 StartY=6.42 StartZ=0 EndX=-38.67 EndY=3.12 EndZ=0
    g10: LineSegment StartX=-38.67 StartY=3.12 StartZ=0 EndX=-44.67 EndY=3.12 EndZ=0
    g11: GeomPoint X=-41.67 Y=4.77 Z=0
    g12: LineSegment StartX=-24.67 StartY=3.12 StartZ=0 EndX=-24.67 EndY=6.42 EndZ=0
    g13: LineSegment StartX=-24.67 StartY=6.42 StartZ=0 EndX=-18.67 EndY=6.42 EndZ=0
    g14: LineSegment StartX=-18.67 StartY=6.42 StartZ=0 EndX=-18.67 EndY=3.12 EndZ=0
    g15: LineSegment StartX=-18.67 StartY=3.12 StartZ=0 EndX=-24.67 EndY=3.12 EndZ=0
    g16: GeomPoint X=-21.67 Y=4.77 Z=0
    g17: LineSegment StartX=-14.67 StartY=3.12 StartZ=0 EndX=-14.67 EndY=6.42 EndZ=0
    g18: LineSegment StartX=-14.67 StartY=6.42 StartZ=0 EndX=-8.67 EndY=6.42 EndZ=0
    g19: LineSegment StartX=-8.67 StartY=6.42 StartZ=0 EndX=-8.67 EndY=3.12 EndZ=0
    g20: LineSegment StartX=-8.67 StartY=3.12 StartZ=0 EndX=-14.67 EndY=3.12 EndZ=0
    g21: GeomPoint X=-11.67 Y=4.77 Z=0
    g22: ArcOfCircle CenterX=-33.17 CenterY=4.77 CenterZ=0 NormalX=0 NormalY=0 NormalZ=1 AngleXU=0 Radius=1.5 StartAngle=1.5708 EndAngle=4.71239
    g23: ArcOfCircle CenterX=-30.17 CenterY=4.77 CenterZ=0 NormalX=0 NormalY=0 NormalZ=1 AngleXU=0 Radius=1.5 StartAngle=4.71239 EndAngle=7.85398
    g24: LineSegment StartX=-33.17 StartY=3.27 StartZ=0 EndX=-30.17 EndY=3.27 EndZ=0
    g25: LineSegment StartX=-30.17 StartY=6.27 StartZ=0 EndX=-33.17 EndY=6.27 EndZ=0
    g26: ArcOfCircle CenterX=-23.17 CenterY=4.77 CenterZ=0 NormalX=0 NormalY=0 NormalZ=1 AngleXU=0 Radius=1.5 StartAngle=1.5708 EndAngle=4.71239
    g27: ArcOfCircle CenterX=-20.17 CenterY=4.77 CenterZ=0 NormalX=0 NormalY=0 NormalZ=1 AngleXU=0 Radius=1.5 StartAngle=4.71239 EndAngle=7.85398
    g28: LineSegment StartX=-23.17 StartY=3.27 StartZ=0 EndX=-20.17 EndY=3.27 EndZ=0
    g29: LineSegment StartX=-20.17 StartY=6.27 StartZ=0 EndX=-23.17 EndY=6.27 EndZ=0
    g30: ArcOfCircle CenterX=-13.17 CenterY=4.77 CenterZ=0 NormalX=0 NormalY=0 NormalZ=1 AngleXU=0 Radius=1.5 StartAngle=1.5708 EndAngle=4.71239
    g31: ArcOfCircle CenterX=-10.17 CenterY=4.77 CenterZ=0 NormalX=0 NormalY=0 NormalZ=1 AngleXU=0 Radius=1.5 StartAngle=4.71239 EndAngle=7.85398
    g32: LineSegment StartX=-13.17 StartY=3.27 StartZ=0 EndX=-10.17 EndY=3.27 EndZ=0
    g33: LineSegment StartX=-10.17 StartY=6.27 StartZ=0 EndX=-13.17 EndY=6.27 EndZ=0
    g34: ArcOfCircle CenterX=-43.17 CenterY=4.77 CenterZ=0 NormalX=0 NormalY=0 NormalZ=1 AngleXU=0 Radius=1.5 StartAngle=1.5708 EndAngle=4.71239
    g35: ArcOfCircle CenterX=-40.17 CenterY=4.77 CenterZ=0 NormalX=0 NormalY=0 NormalZ=1 AngleXU=0 Radius=1.5 StartAngle=4.71239 EndAngle=7.85398
    g36: LineSegment StartX=-43.17 StartY=3.27 StartZ=0 EndX=-40.17 EndY=3.27 EndZ=0
    g37: LineSegment StartX=-40.17 StartY=6.27 StartZ=0 EndX=-43.17 EndY=6.27 EndZ=0
    g38: GeomPoint X=-26.67 Y=11.37 Z=0
  constraints (94):
    c: Horizontal(g0)
    c: DistanceX(g0,g0) = 40.8
    c: Symmetric(g0,g0,g1)
    c: DistanceX(g1,g-1) = 26.67
    c: Coincident(g2,g3)
    c: Coincident(g3,g4)
    c: Coincident(g4,g5)
    c: Coincident(g5,g2)
    c: Horizontal(g3)
    c: Horizontal(g5)
    c: Vertical(g2)
    c: Vertical(g4)
    c: Symmetric(g3,g2,g6)
    c: PointOnObject(g6,g0)
    c: Coincident(g7,g8)
    c: Coincident(g8,g9)
    c: Coincident(g9,g10)
    c: Coincident(g10,g7)
    c: Horizontal(g8)
    c: Horizontal(g10)
    c: Vertical(g7)
    c: Vertical(g9)
    c: Symmetric(g8,g7,g11)
    c: PointOnObject(g11,g0)
    c: Coincident(g12,g13)
    c: Coincident(g13,g14)
    c: Coincident(g14,g15)
    c: Coincident(g15,g12)
    c: Horizontal(g13)
    c: Horizontal(g15)
    c: Vertical(g12)
    c: Vertical(g14)
    c: Symmetric(g13,g12,g16)
    c: Coincident(g17,g18)
    c: Coincident(g18,g19)
    c: Coincident(g19,g20)
    c: Coincident(g20,g17)
    c: Horizontal(g18)
    c: Horizontal(g20)
    c: Vertical(g17)
    c: Vertical(g19)
    c: Symmetric(g18,g17,g21)
    c: Symmetric(g16,g6,g1)
    c: Symmetric(g11,g21,g1)
    c: Equal(g13,g3)
    c: Equal(g3,g8)
    c: Equal(g8,g18)
    c: Equal(g14,g17)
    c: Equal(g17,g4)
    c: Equal(g4,g9)
    c: DistanceX(g13,g13) = 6
    c: DistanceY(g19,g19) = 3.3
    c: DistanceX(g4,g12) = 4
    c: DistanceX(g14,g17) = 4
    c: Tangent(g22,g24) = -1.5708
    c: Tangent(g24,g23) = -1.5708
    c: Tangent(g23,g25) = -1.5708
    c: Tangent(g25,g22) = -1.5708
    c: Equal(g22,g23)
    c: PointOnObject(g22,g0)
    c: Tangent(g26,g28) = -1.5708
    c: Tangent(g28,g27) = -1.5708
    c: Tangent(g27,g29) = -1.5708
    c: Tangent(g29,g26) = -1.5708
    c: Equal(g26,g27)
    c: PointOnObject(g26,g0)
    c: Tangent(g30,g32) = -1.5708
    c: Tangent(g32,g31) = -1.5708
    c: Tangent(g31,g33) = -1.5708
    c: Tangent(g33,g30) = -1.5708
    c: Equal(g30,g31)
    c: PointOnObject(g30,g0)
    c: Tangent(g34,g36) = -1.5708
    c: Tangent(g36,g35) = -1.5708
    c: Tangent(g35,g37) = -1.5708
    c: Tangent(g37,g34) = -1.5708
    c: Equal(g34,g35)
    c: PointOnObject(g34,g0)
    c: Equal(g35,g23)
    c: Equal(g23,g27)
    c: Equal(g27,g31)
    c: Equal(g29,g33)
    c: Equal(g33,g25)
    c: Equal(g25,g37)
    c: Symmetric(g34,g35,g11)
    c: Symmetric(g22,g23,g6)
    c: Symmetric(g26,g27,g16)
    c: Symmetric(g30,g31,g21)
    c: Diameter(g31) = 3
    c: DistanceX(g33,g33) = 3
    c: DistanceY(g-1,g38) = 11.37
    c: Vertical(g38,g1)
    c: DistanceY(g23,g38) = 5.1
    c: DistanceY(g-1,g0) = 4.77
FEATURE [PartDesign::Pocket] Pocket010  label="TEK1_button"
  BaseFeature = -> Pocket008
  Direction = (0,0,-1)
  Length = 5
  Length2 = 5
  Profile = -> Sketch029
  ReferenceAxis = -> Sketch029 [N_Axis]
  Type = 0
FEATURE [TechDraw::DrawSVGTemplate] Template002
  Height = 210
  Orientation = 1
  Template = C:/Program Files/FreeCAD 0.21/data/Mod/TechDraw/Templates/A4_Landscape_blank.svg
  Width = 297
FEATURE [Sketcher::SketchObject] Sketch030  label="TEK2_ButtonHole001"
  FullyConstrained = true
  MapMode = 5
  Support = -> [XY_Plane011]
  sketch-geometry (96):
    g0: Circle CenterX=-40.005 CenterY=-13.335 CenterZ=0 NormalX=0 NormalY=0 NormalZ=1 AngleXU=0 Radius=2
    g1: Circle CenterX=-13.335 CenterY=-13.335 CenterZ=0 NormalX=0 NormalY=0 NormalZ=1 AngleXU=0 Radius=2
    g2: LineSegment StartX=-40.005 StartY=-13.335 StartZ=0 EndX=-13.335 EndY=-13.335 EndZ=0
    g3: Circle CenterX=13.335 CenterY=-13.335 CenterZ=0 NormalX=0 NormalY=0 NormalZ=1 AngleXU=0 Radius=2
    g4: LineSegment StartX=-13.335 StartY=-13.335 StartZ=0 EndX=13.335 EndY=-13.335 EndZ=0
    g5: Circle CenterX=40.005 CenterY=-13.335 CenterZ=0 NormalX=0 NormalY=0 NormalZ=1 AngleXU=0 Radius=2
    g6: LineSegment StartX=13.335 StartY=-13.335 StartZ=0 EndX=40.005 EndY=-13.335 EndZ=0
    g7: Circle CenterX=-40.005 CenterY=-40.005 CenterZ=0 NormalX=0 NormalY=0 NormalZ=1 AngleXU=0 Radius=2
    g8: LineSegment StartX=-40.005 StartY=-13.335 StartZ=0 EndX=-40.005 EndY=-40.005 EndZ=0
    g9: Circle CenterX=-13.335 CenterY=-40.005 CenterZ=0 NormalX=0 NormalY=0 NormalZ=1 AngleXU=0 Radius=2
    g10: LineSegment StartX=-40.005 StartY=-40.005 StartZ=0 EndX=-13.335 EndY=-40.005 EndZ=0
    g11: Circle CenterX=13.335 CenterY=-40.005 CenterZ=0 NormalX=0 NormalY=0 NormalZ=1 AngleXU=0 Radius=2
    g12: LineSegment StartX=-13.335 StartY=-40.005 StartZ=0 EndX=13.335 EndY=-40.005 EndZ=0
    g13: Circle CenterX=40.005 CenterY=-40.005 CenterZ=0 NormalX=0 NormalY=0 NormalZ=1 AngleXU=0 Radius=2
    g14: LineSegment StartX=13.335 StartY=-40.005 StartZ=0 EndX=40.005 EndY=-40.005 EndZ=0
    g15: LineSegment StartX=0 StartY=0 StartZ=0 EndX=13.335 EndY=-13.335 EndZ=0
    g16: LineSegment StartX=0 StartY=0 StartZ=0 EndX=-13.335 EndY=-13.335 EndZ=0
    g17: LineSegment StartX=-48.505 StartY=-19.735 StartZ=0 EndX=-48.505 EndY=-6.935 EndZ=0
    g18: LineSegment StartX=-46.405 StartY=-4.835 StartZ=0 EndX=-33.605 EndY=-4.835 EndZ=0
    g19: LineSegment StartX=-31.505 StartY=-6.935 StartZ=0 EndX=-31.505 EndY=-19.735 EndZ=0
    g20: LineSegment StartX=-33.605 StartY=-21.835 StartZ=0 EndX=-46.405 EndY=-21.835 EndZ=0
    g21: GeomPoint X=-40.005 Y=-13.335 Z=0
    g22: LineSegment StartX=-21.835 StartY=-19.735 StartZ=0 EndX=-21.835 EndY=-6.935 EndZ=0
    g23: LineSegment StartX=-19.735 StartY=-4.835 StartZ=0 EndX=-6.935 EndY=-4.835 EndZ=0
    g24: LineSegment StartX=-4.835 StartY=-6.935 StartZ=0 EndX=-4.835 EndY=-19.735 EndZ=0
    g25: LineSegment StartX=-6.935 StartY=-21.835 StartZ=0 EndX=-19.735 EndY=-21.835 EndZ=0
    g26: GeomPoint X=-13.335 Y=-13.335 Z=0
    g27: LineSegment StartX=4.835 StartY=-19.735 StartZ=0 EndX=4.835 EndY=-6.935 EndZ=0
    g28: LineSegment StartX=6.935 StartY=-4.835 StartZ=0 EndX=19.735 EndY=-4.835 EndZ=0
    g29: LineSegment StartX=21.835 StartY=-6.935 StartZ=0 EndX=21.835 EndY=-19.735 EndZ=0
    g30: LineSegment StartX=19.735 StartY=-21.835 StartZ=0 EndX=6.935 EndY=-21.835 EndZ=0
    g31: GeomPoint X=13.335 Y=-13.335 Z=0
    g32: LineSegment StartX=31.505 StartY=-19.735 StartZ=0 EndX=31.505 EndY=-6.935 EndZ=0
    g33: LineSegment StartX=33.605 StartY=-4.835 StartZ=0 EndX=46.405 EndY=-4.835 EndZ=0
    g34: LineSegment StartX=48.505 StartY=-6.935 StartZ=0 EndX=48.505 EndY=-19.735 EndZ=0
    g35: LineSegment StartX=46.405 StartY=-21.835 StartZ=0 EndX=33.605 EndY=-21.835 EndZ=0
    g36: GeomPoint X=40.005 Y=-13.335 Z=0
    g37: LineSegment StartX=31.505 StartY=-46.405 StartZ=0 EndX=31.505 EndY=-33.605 EndZ=0
    g38: LineSegment StartX=33.605 StartY=-31.505 StartZ=0 EndX=46.405 EndY=-31.505 EndZ=0
    g39: LineSegment StartX=48.505 StartY=-33.605 StartZ=0 EndX=48.505 EndY=-46.405 EndZ=0
    g40: LineSegment StartX=46.405 StartY=-48.505 StartZ=0 EndX=33.605 EndY=-48.505 EndZ=0
    g41: GeomPoint X=40.005 Y=-40.005 Z=0
    g42: LineSegment StartX=4.835 StartY=-46.405 StartZ=0 EndX=4.835 EndY=-33.605 EndZ=0
    g43: LineSegment StartX=6.935 StartY=-31.505 StartZ=0 EndX=19.735 EndY=-31.505 EndZ=0
    g44: LineSegment StartX=21.835 StartY=-33.605 StartZ=0 EndX=21.835 EndY=-46.405 EndZ=0
    g45: LineSegment StartX=19.735 StartY=-48.505 StartZ=0 EndX=6.935 EndY=-48.505 EndZ=0
    g46: GeomPoint X=13.335 Y=-40.005 Z=0
    g47: LineSegment StartX=-21.835 StartY=-46.405 StartZ=0 EndX=-21.835 EndY=-33.605 EndZ=0
    g48: LineSegment StartX=-19.735 StartY=-31.505 StartZ=0 EndX=-6.935 EndY=-31.505 EndZ=0
    g49: LineSegment StartX=-4.835 StartY=-33.605 StartZ=0 EndX=-4.835 EndY=-46.405 EndZ=0
    g50: LineSegment StartX=-6.935 StartY=-48.505 StartZ=0 EndX=-19.735 EndY=-48.505 EndZ=0
    g51: GeomPoint X=-13.335 Y=-40.005 Z=0
    g52: LineSegment StartX=-48.505 StartY=-46.405 StartZ=0 EndX=-48.505 EndY=-33.605 EndZ=0
    g53: LineSegment StartX=-46.405 StartY=-31.505 StartZ=0 EndX=-33.605 EndY=-31.505 EndZ=0
    g54: LineSegment StartX=-31.505 StartY=-33.605 StartZ=0 EndX=-31.505 EndY=-46.405 EndZ=0
    g55: LineSegment StartX=-33.605 StartY=-48.505 StartZ=0 EndX=-46.405 EndY=-48.505 EndZ=0
    g56: GeomPoint X=-40.005 Y=-40.005 Z=0
    g57: ArcOfCircle CenterX=-46.405 CenterY=-6.935 CenterZ=0 NormalX=0 NormalY=0 NormalZ=1 AngleXU=0 Radius=2.1 StartAngle=1.5708 EndAngle=3.14159
    g58: ArcOfCircle CenterX=-46.405 CenterY=-19.735 CenterZ=0 NormalX=0 NormalY=0 NormalZ=1 AngleXU=0 Radius=2.1 StartAngle=3.14159 EndAngle=4.71239
    g59: ArcOfCircle CenterX=-33.605 CenterY=-19.735 CenterZ=0 NormalX=0 NormalY=0 NormalZ=1 AngleXU=0 Radius=2.1 StartAngle=4.71239 EndAngle=6.28319
    g60: ArcOfCircle CenterX=-33.605 CenterY=-6.935 CenterZ=0 NormalX=0 NormalY=0 NormalZ=1 AngleXU=0 Radius=2.1 StartAngle=0 EndAngle=1.5708
    g61: ArcOfCircle CenterX=-19.735 CenterY=-6.935 CenterZ=0 NormalX=0 NormalY=0 NormalZ=1 AngleXU=0 Radius=2.1 StartAngle=1.5708 EndAngle=3.14159
    g62: ArcOfCircle CenterX=-19.735 CenterY=-19.735 CenterZ=0 NormalX=0 NormalY=0 NormalZ=1 AngleXU=0 Radius=2.1 StartAngle=3.14159 EndAngle=4.71239
    g63: ArcOfCircle CenterX=-6.935 CenterY=-19.735 CenterZ=0 NormalX=0 NormalY=0 NormalZ=1 AngleXU=0 Radius=2.1 StartAngle=4.71239 EndAngle=6.28319
    g64: ArcOfCircle CenterX=-6.935 CenterY=-6.935 CenterZ=0 NormalX=0 NormalY=0 NormalZ=1 AngleXU=0 Radius=2.1 StartAngle=0 EndAngle=1.5708
    g65: ArcOfCircle CenterX=6.935 CenterY=-6.935 CenterZ=0 NormalX=0 NormalY=0 NormalZ=1 AngleXU=0 Radius=2.1 StartAngle=1.5708 EndAngle=3.14159
    g66: ArcOfCircle CenterX=19.735 CenterY=-6.935 CenterZ=0 NormalX=0 NormalY=0 NormalZ=1 AngleXU=0 Radius=2.1 StartAngle=0 EndAngle=1.5708
    g67: ArcOfCircle CenterX=19.735 CenterY=-19.735 CenterZ=0 NormalX=0 NormalY=0 NormalZ=1 AngleXU=0 Radius=2.1 StartAngle=4.71239 EndAngle=6.28319
    g68: ArcOfCircle CenterX=6.935 CenterY=-19.735 CenterZ=0 NormalX=0 NormalY=0 NormalZ=1 AngleXU=0 Radius=2.1 StartAngle=3.14159 EndAngle=4.71239
    g69: ArcOfCircle CenterX=33.605 CenterY=-6.935 CenterZ=0 NormalX=0 NormalY=0 NormalZ=1 AngleXU=0 Radius=2.1 StartAngle=1.5708 EndAngle=3.14159
    g70: ArcOfCircle CenterX=46.405 CenterY=-6.935 CenterZ=0 NormalX=0 NormalY=0 NormalZ=1 AngleXU=0 Radius=2.1 StartAngle=0 EndAngle=1.5708
    g71: ArcOfCircle CenterX=33.605 CenterY=-19.735 CenterZ=0 NormalX=0 NormalY=0 NormalZ=1 AngleXU=0 Radius=2.1 StartAngle=3.14159 EndAngle=4.71239
    g72: ArcOfCircle CenterX=46.405 CenterY=-19.735 CenterZ=0 NormalX=0 NormalY=0 NormalZ=1 AngleXU=0 Radius=2.1 StartAngle=4.71239 EndAngle=6.28319
    g73: ArcOfCircle CenterX=33.605 CenterY=-33.605 CenterZ=0 NormalX=0 NormalY=0 NormalZ=1 AngleXU=0 Radius=2.1 StartAngle=1.5708 EndAngle=3.14159
    g74: ArcOfCircle CenterX=46.405 CenterY=-33.605 CenterZ=0 NormalX=0 NormalY=0 NormalZ=1 AngleXU=0 Radius=2.1 StartAngle=-9e-16 EndAngle=1.5708
    g75: ArcOfCircle CenterX=46.405 CenterY=-46.405 CenterZ=0 NormalX=0 NormalY=0 NormalZ=1 AngleXU=0 Radius=2.1 StartAngle=4.71239 EndAngle=6.28319
    g76: ArcOfCircle CenterX=33.605 CenterY=-46.405 CenterZ=0 NormalX=0 NormalY=0 NormalZ=1 AngleXU=0 Radius=2.1 StartAngle=3.14159 EndAngle=4.71239
    g77: ArcOfCircle CenterX=6.935 CenterY=-33.605 CenterZ=0 NormalX=0 NormalY=0 NormalZ=1 AngleXU=0 Radius=2.1 StartAngle=1.5708 EndAngle=3.14159
    g78: ArcOfCircle CenterX=19.735 CenterY=-33.605 CenterZ=0 NormalX=0 NormalY=0 NormalZ=1 AngleXU=0 Radius=2.1 StartAngle=-9e-16 EndAngle=1.5708
    g79: ArcOfCircle CenterX=19.735 CenterY=-46.405 CenterZ=0 NormalX=0 NormalY=0 NormalZ=1 AngleXU=0 Radius=2.1 StartAngle=4.71239 EndAngle=6.28319
    g80: ArcOfCircle CenterX=6.935 CenterY=-46.405 CenterZ=0 NormalX=0 NormalY=0 NormalZ=1 AngleXU=0 Radius=2.1 StartAngle=3.14159 EndAngle=4.71239
    g81: ArcOfCircle CenterX=-19.735 CenterY=-33.605 CenterZ=0 NormalX=0 NormalY=0 NormalZ=1 AngleXU=0 Radius=2.1 StartAngle=1.5708 EndAngle=3.14159
    g82: ArcOfCircle CenterX=-6.935 CenterY=-33.605 CenterZ=0 NormalX=0 NormalY=0 NormalZ=1 AngleXU=0 Radius=2.1 StartAngle=1.5e-15 EndAngle=1.5708
    g83: ArcOfCircle CenterX=-6.935 CenterY=-46.405 CenterZ=0 NormalX=0 NormalY=0 NormalZ=1 AngleXU=0 Radius=2.1 StartAngle=4.71239 EndAngle=6.28319
    g84: ArcOfCircle CenterX=-19.735 CenterY=-46.405 CenterZ=0 NormalX=0 NormalY=0 NormalZ=1 AngleXU=0 Radius=2.1 StartAngle=3.14159 EndAngle=4.71239
    g85: ArcOfCircle CenterX=-46.405 CenterY=-33.605 CenterZ=0 NormalX=0 NormalY=0 NormalZ=1 AngleXU=0 Radius=2.1 StartAngle=1.5708 EndAngle=3.14159
    g86: ArcOfCircle CenterX=-33.605 CenterY=-33.605 CenterZ=0 NormalX=0 NormalY=0 NormalZ=1 AngleXU=0 Radius=2.1 StartAngle=-9e-16 EndAngle=1.5708
    g87: ArcOfCircle CenterX=-33.605 CenterY=-46.405 CenterZ=0 NormalX=0 NormalY=0 NormalZ=1 AngleXU=0 Radius=2.1 StartAngle=4.71239 EndAngle=6.28319
    g88: ArcOfCircle CenterX=-46.405 CenterY=-46.405 CenterZ=0 NormalX=0 NormalY=0 NormalZ=1 AngleXU=0 Radius=2.1 StartAngle=3.14159 EndAngle=4.71239
    g89: LineSegment StartX=-13.335 StartY=-4.835 StartZ=0 EndX=-13.335 EndY=-21.835 EndZ=0
    g90: LineSegment StartX=13.335 StartY=-4.835 StartZ=0 EndX=13.335 EndY=-21.835 EndZ=0
    g91: LineSegment StartX=40.005 StartY=-4.835 StartZ=0 EndX=40.005 EndY=-21.835 EndZ=0
    g92: LineSegment StartX=40.005 StartY=-31.505 StartZ=0 EndX=40.005 EndY=-48.505 EndZ=0
    g93: LineSegment StartX=13.335 StartY=-31.505 StartZ=0 EndX=13.335 EndY=-48.505 EndZ=0
    g94: LineSegment StartX=-13.335 StartY=-31.505 StartZ=0 EndX=-13.335 EndY=-48.505 EndZ=0
    g95: LineSegment StartX=-40.005 StartY=-31.505 StartZ=0 EndX=-40.005 EndY=-48.505 EndZ=0
  constraints (222):
    c: Diameter(g0) = 4
    c: Coincident(g0,g2)
    c: Coincident(g1,g2)
    c: Coincident(g1,g4)
    c: Coincident(g3,g4)
    c: Coincident(g3,g6)
    c: Coincident(g5,g6)
    c: Coincident(g0,g8)
    c: Coincident(g7,g8)
    c: Coincident(g7,g10)
    c: Coincident(g9,g10)
    c: Coincident(g9,g12)
    c: Coincident(g11,g12)
    c: Coincident(g11,g14)
    c: Coincident(g13,g14)
    c: Coincident(g-1,g16)
    c: Coincident(g16,g1)
    c: Coincident(g15,g3)
    c: Horizontal(g4)
    c: Horizontal(g2)
    c: Horizontal(g6)
    c: Horizontal(g10)
    c: Horizontal(g12)
    c: Horizontal(g14)
    c: Vertical(g8)
    c: Equal(g8,g2)
    c: Equal(g2,g10)
    c: Equal(g10,g12)
    c: Equal(g12,g4)
    c: Equal(g4,g6)
    c: Equal(g6,g14)
    c: DistanceX(g4,g4) = 26.67
    c: Equal(g16,g15)
    c: Coincident(g15,g16)
    c: Perpendicular(g15,g16)
    c: Equal(g7,g9)
    c: Equal(g9,g11)
    c: Equal(g11,g13)
    c: Equal(g13,g5)
    c: Equal(g5,g3)
    c: Equal(g3,g1)
    c: Equal(g1,g0)
    c: Horizontal(g18)
    c: Vertical(g17)
    c: Coincident(g21,g0)
    c: Horizontal(g23)
    c: Horizontal(g25)
    c: Vertical(g22)
    c: Coincident(g26,g1)
    c: Horizontal(g28)
    c: Horizontal(g30)
    c: Vertical(g27)
    c: Vertical(g29)
    c: Coincident(g31,g3)
    c: Horizontal(g33)
    c: Horizontal(g35)
    c: Vertical(g32)
    c: Vertical(g34)
    c: Coincident(g36,g5)
    c: Horizontal(g38)
    c: Horizontal(g40)
    c: Vertical(g37)
    c: Vertical(g39)
    c: Coincident(g41,g13)
    c: Horizontal(g43)
    c: Horizontal(g45)
    c: Vertical(g42)
    c: Vertical(g44)
    c: Coincident(g46,g11)
    c: Horizontal(g48)
    c: Horizontal(g50)
    c: Vertical(g47)
    c: Vertical(g49)
    c: Coincident(g51,g9)
    c: Horizontal(g53)
    c: Horizontal(g55)
    c: Vertical(g52)
    c: Vertical(g54)
    c: Coincident(g56,g7)
    c: Tangent(g17,g57) = 1.5708
    c: Tangent(g18,g57) = 1.5708
    c: Tangent(g17,g58) = 1.5708
    c: Tangent(g20,g58) = 1.5708
    c: Tangent(g19,g59) = 1.5708
    c: Tangent(g20,g59) = 1.5708
    c: Tangent(g19,g60) = 1.5708
    c: Tangent(g18,g60) = 1.5708
    c: Tangent(g23,g61) = 1.5708
    c: Tangent(g22,g61) = 1.5708
    c: Tangent(g22,g62) = 1.5708
    c: Tangent(g25,g62) = 1.5708
    c: Tangent(g24,g63) = 1.5708
    c: Tangent(g25,g63) = 1.5708
    c: Tangent(g23,g64) = 1.5708
    c: Tangent(g24,g64) = 1.5708
    c: Tangent(g28,g65) = 1.5708
    c: Tangent(g27,g65) = 1.5708
    c: Tangent(g29,g66) = 1.5708
    c: Tangent(g28,g66) = 1.5708
    c: Tangent(g29,g67) = 1.5708
    c: Tangent(g30,g67) = 1.5708
    c: Tangent(g27,g68) = 1.5708
    c: Tangent(g30,g68) = 1.5708
    c: Tangent(g33,g69) = 1.5708
    c: Tangent(g32,g69) = 1.5708
    c: Tangent(g33,g70) = 1.5708
    c: Tangent(g34,g70) = 1.5708
    c: Tangent(g32,g71) = 1.5708
    c: Tangent(g35,g71) = 1.5708
    c: Tangent(g34,g72) = 1.5708
    c: Tangent(g35,g72) = 1.5708
    c: Tangent(g38,g73) = 1.5708
    c: Tangent(g37,g73) = 1.5708
    c: Tangent(g38,g74) = 1.5708
    c: Tangent(g39,g74) = 1.5708
    c: Tangent(g39,g75) = 1.5708
    c: Tangent(g40,g75) = 1.5708
    c: Tangent(g37,g76) = 1.5708
    c: Tangent(g40,g76) = 1.5708
    c: Tangent(g43,g77) = 1.5708
    c: Tangent(g42,g77) = 1.5708
    c: Tangent(g43,g78) = 1.5708
    c: Tangent(g44,g78) = 1.5708
    c: Tangent(g44,g79) = 1.5708
    c: Tangent(g45,g79) = 1.5708
    c: Tangent(g42,g80) = 1.5708
    c: Tangent(g45,g80) = 1.5708
    c: Tangent(g48,g81) = 1.5708
    c: Tangent(g47,g81) = 1.5708
    c: Tangent(g48,g82) = 1.5708
    c: Tangent(g49,g82) = 1.5708
    c: Tangent(g49,g83) = 1.5708
    c: Tangent(g50,g83) = 1.5708
    c: Tangent(g47,g84) = 1.5708
    c: Tangent(g50,g84) = 1.5708
    c: Tangent(g52,g85) = 1.5708
    c: Tangent(g53,g85) = 1.5708
    c: Tangent(g53,g86) = 1.5708
    c: Tangent(g54,g86) = 1.5708
    c: Tangent(g54,g87) = 1.5708
    c: Tangent(g55,g87) = 1.5708
    c: Tangent(g52,g88) = 1.5708
    c: Tangent(g55,g88) = 1.5708
    c: Equal(g57,g58)
    c: Equal(g58,g60)
    c: Equal(g60,g59)
    c: Equal(g59,g62)
    c: Equal(g62,g61)
    c: Equal(g61,g64)
    c: Equal(g64,g63)
    c: Equal(g63,g68)
    c: Equal(g68,g65)
    c: Equal(g65,g66)
    c: Equal(g66,g67)
    c: Equal(g67,g71)
    c: Equal(g71,g69)
    c: Equal(g69,g70)
    c: Equal(g70,g72)
    c: Equal(g72,g73)
    c: Equal(g73,g74)
    c: Equal(g74,g75)
    c: Equal(g75,g76)
    c: Equal(g76,g79)
    c: Equal(g79,g80)
    c: Equal(g80,g77)
    c: Equal(g77,g78)
    c: Equal(g78,g82)
    c: Equal(g82,g81)
    c: Equal(g81,g83)
    c: Equal(g83,g84)
    c: Equal(g84,g87)
    c: Equal(g87,g88)
    c: Equal(g88,g85)
    c: Equal(g85,g86)
    c: Diameter(g57) = 4.2
    c: Equal(g19,g20)
    c: Symmetric(g19,g19,g2)
    c: Symmetric(g20,g20,g8)
    c: Symmetric(g24,g24,g4)
    c: PointOnObject(g89,g25)
    c: Vertical(g89)
    c: PointOnObject(g90,g30)
    c: Vertical(g90)
    c: PointOnObject(g91,g35)
    c: Vertical(g91)
    c: PointOnObject(g93,g45)
    c: PointOnObject(g94,g50)
    c: Vertical(g94)
    c: PointOnObject(g95,g55)
    c: Vertical(g95)
    c: Symmetric(g23,g23,g89)
    c: PointOnObject(g1,g89)
    c: Symmetric(g28,g28,g90)
    c: Symmetric(g33,g33,g91)
    c: PointOnObject(g92,g40)
    c: Vertical(g92)
    c: Symmetric(g38,g38,g92)
    c: Vertical(g93)
    c: Symmetric(g43,g43,g93)
    c: Symmetric(g48,g48,g94)
    c: Symmetric(g53,g53,g95)
    c: Equal(g19,g25)
    c: Equal(g25,g24)
    c: Equal(g24,g30)
    c: Equal(g30,g29)
    c: Equal(g29,g35)
    c: Equal(g35,g34)
    c: Equal(g34,g40)
    c: Equal(g40,g39)
    c: Equal(g39,g45)
    c: Equal(g45,g44)
    c: Equal(g44,g54)
    c: Equal(g54,g55)
    c: Equal(g55,g49)
    c: Equal(g49,g50)
    c: Symmetric(g94,g94,g9)
    c: Symmetric(g95,g95,g7)
    c: Symmetric(g93,g93,g11)
    c: Symmetric(g92,g92,g13)
    c: Symmetric(g91,g91,g5)
    c: Symmetric(g90,g90,g3)
    c: DistanceY(g20,g18) = 17
FEATURE [PartDesign::Pocket] Pocket011  label="TEK1_Buttonhole"
  BaseFeature = -> Pocket010
  Direction = (0,0,-1)
  Length = 5
  Length2 = 5
  Profile = -> Sketch030
  ReferenceAxis = -> Sketch030 [N_Axis]
  Type = 1
FEATURE [PartDesign::Body] Body011  label="FRONTPANEL-SHEET-VSN1"
  BaseFeature = -> Body
  Group = -> [Clone009,Sketch023,Sketch024,Sketch025,Pocket007,Sketch026,Sketch027,Pocket008,Sketch028,Sketch029,Pocket010,Sketch030,Pocket011]
  Origin = -> Origin011
  Tip = -> Pocket011
FEATURE [TechDraw::DrawSVGTemplate] Template
  EditableTexts = COLOR=Anodized matte black - RAL code: 9004; CreationDate=2024/07/29; E.G.APPROVED=PRELIMINARY; FC-Scale=1:1; FC-Title=VSN1-frontpanel; IntechStudioLtd.=Intech Studio Ltd.; MATERIAL=Aluminum 5052-H32; REV=01; STANDARD=ISO 2768 - m
  Height = 297
  Orientation = 1
  Template = <userpath>/Documents/grid-hardware/Manufacturing/FreeCAD_technical_drawing_template/A3_LandscapeTD_MODIFIED.svg
  Width = 420
FEATURE [TechDraw::DrawViewPart] View004
  CoarseView = false
  Direction = (0,0,1)
  Focus = 100
  HardHidden = false
  IsoCount = 0
  IsoHidden = false
  IsoVisible = true
  LockPosition = false
  Perspective = false
  Rotation = 0
  ScaleType = 0
  ScrubCount = 0
  SeamHidden = false
  SeamVisible = true
  SmoothHidden = false
  SmoothVisible = true
  Source = -> [Body011]
  X = 148.5
  XDirection = (1,3e-06,0)
  Y = 105
FEATURE [TechDraw::DrawPage] Page002  label="VSN1_dxf"
  KeepUpdated = true
  NextBalloonIndex = 1
  ProjectionType = 0
  Template = -> Template002
  Views = -> [View004]
FEATURE [TechDraw::DrawViewPart] View005
  CoarseView = false
  Direction = (0,1e-06,-1)
  Focus = 100
  HardHidden = false
  IsoCount = 0
  IsoHidden = false
  IsoVisible = true
  LockPosition = false
  Perspective = false
  Rotation = 0
  ScaleType = 2
  ScrubCount = 0
  SeamHidden = false
  SeamVisible = true
  SmoothHidden = false
  SmoothVisible = true
  Source = -> [Body011]
  X = 318.888
  XDirection = (-1,-0.0008,-8e-10)
  Y = 196.926
FEATURE [TechDraw::DrawViewPart] View006
  CoarseView = false
  Direction = (-1,-0.0008,-1e-06)
  Focus = 100
  HardHidden = false
  IsoCount = 0
  IsoHidden = false
  IsoVisible = true
  LockPosition = false
  Perspective = false
  Rotation = 0
  ScaleType = 0
  ScrubCount = 0
  SeamHidden = false
  SeamVisible = true
  SmoothHidden = false
  SmoothVisible = true
  Source = -> [Body011]
  X = 222.176
  XDirection = (-9.992e-07,-1.0008e-06,1)
  Y = 196.82
FEATURE [TechDraw::DrawViewPart] View007
  CoarseView = false
  Direction = (0.57735,0.57735,0.57735)
  Focus = 100
  HardHidden = false
  IsoCount = 0
  IsoHidden = false
  IsoVisible = true
  LockPosition = false
  Perspective = false
  Rotation = 0
  Scale = 0.5
  ScaleType = 2
  ScrubCount = 0
  SeamHidden = false
  SeamVisible = true
  SmoothHidden = false
  SmoothVisible = true
  Source = -> [Body011]
  X = 178.74
  XDirection = (0.707107,0,-0.707107)
  Y = 78.2733
FEATURE [TechDraw::DrawHatch] Hatch  label="HatchF1"
  HatchPattern = C:/Program Files/FreeCAD 0.21/data/Mod/TechDraw/Patterns/solid.svg
  Source = -> View007 [Face1]
FEATURE [TechDraw::DrawViewPart] View
  CoarseView = false
  Direction = (0,-1e-06,1)
  Focus = 100
  HardHidden = false
  IsoCount = 0
  IsoHidden = false
  IsoVisible = true
  LockPosition = false
  Perspective = false
  Rotation = 0
  ScaleType = 2
  ScrubCount = 0
  SeamHidden = false
  SeamVisible = true
  SmoothHidden = false
  SmoothVisible = true
  Source = -> [Body011]
  X = 126.1
  XDirection = (1,0.0008,8e-10)
  Y = 195.983
FEATURE [TechDraw::DrawViewDimension] Dimension001
  AngleOverride = false
  Arbitrary = false
  ArbitraryTolerances = false
  EqualTolerance = true
  ExtensionAngle = 0
  FormatSpec = %.2w
  FormatSpecOverTolerance = %+.2w
  FormatSpecUnderTolerance = %+.2w
  Inverted = false
  LineAngle = 0
  LockPosition = false
  MeasureType = 1
  OverTolerance = 0
  References2D = -> [View]
  Rotation = 0
  ScaleType = 0
  TheoreticalExact = false
  Type = 1
  UnderTolerance = 0
  X = -26.5605
  Y = 64.3969
FEATURE [TechDraw::DrawViewDimension] Dimension002
  AngleOverride = false
  Arbitrary = false
  ArbitraryTolerances = false
  EqualTolerance = true
  ExtensionAngle = 0
  FormatSpec = %.2w
  FormatSpecOverTolerance = %+.2w
  FormatSpecUnderTolerance = %+.2w
  Inverted = false
  LineAngle = 0
  LockPosition = false
  MeasureType = 1
  OverTolerance = 0
  References2D = -> [View]
  Rotation = 0
  ScaleType = 0
  TheoreticalExact = false
  Type = 2
  UnderTolerance = 0
  X = -68.3047
  Y = 29.4701
FEATURE [TechDraw::DrawViewBalloon] Balloon
  BubbleShape = 6
  EndType = 0
  EndTypeScale = 1
  KinkLength = 5
  LockPosition = false
  OriginX = -48.5853
  OriginY = 9.71887
  Rotation = 0
  ScaleType = 0
  ShapeScale = 1
  SourceView = -> View
  Text = ⌓|0.2|A|B|C
  TextWrapLen = -1
  X = -87.3779
  Y = 1.5223
FEATURE [TechDraw::DrawViewDimension] Dimension
  AngleOverride = false
  Arbitrary = false
  ArbitraryTolerances = false
  EqualTolerance = true
  ExtensionAngle = 0
  FormatSpec = 4× R%.2w
  FormatSpecOverTolerance = %+.2w
  FormatSpecUnderTolerance = %+.2w
  Inverted = false
  LineAngle = 0
  LockPosition = false
  MeasureType = 1
  OverTolerance = 0
  References2D = -> [View005]
  Rotation = 0
  ScaleType = 0
  TheoreticalExact = false
  Type = 4
  UnderTolerance = 0
  X = 68.3789
  Y = 64.5254
FEATURE [TechDraw::DrawViewDimension] Dimension003
  AngleOverride = false
  Arbitrary = false
  ArbitraryTolerances = false
  EqualTolerance = true
  ExtensionAngle = 0
  FormatSpec = 4× R%.2w
  FormatSpecOverTolerance = %+.2w
  FormatSpecUnderTolerance = %+.2w
  Inverted = false
  LineAngle = 0
  LockPosition = false
  MeasureType = 1
  OverTolerance = 0
  References2D = -> [View]
  Rotation = 0
  ScaleType = 0
  TheoreticalExact = false
  Type = 4
  UnderTolerance = 0
  X = -70.8441
  Y = 65.6784
FEATURE [TechDraw::DrawViewBalloon] Balloon001
  BubbleShape = 6
  EndType = 6
  EndTypeScale = 1
  KinkLength = -0.1
  LockPosition = false
  OriginX = 0.694664
  OriginY = 33.3253
  Rotation = 0
  ScaleType = 0
  ShapeScale = 1
  SourceView = -> View006
  Text = A
  TextWrapLen = -1
  X = 18.2395
  Y = 33.2296
FEATURE [TechDraw::DrawViewBalloon] Balloon002
  BubbleShape = 6
  EndType = 0
  EndTypeScale = 1
  KinkLength = -0.1
  LockPosition = false
  OriginX = 0.748178
  OriginY = 12.2805
  Rotation = 0
  ScaleType = 0
  ShapeScale = 1
  SourceView = -> View006
  Text = ⏥| 0,2
  TextWrapLen = -1
  X = 22.9554
  Y = 12.5321
FEATURE [TechDraw::DrawViewDimension] Dimension004
  AngleOverride = false
  Arbitrary = false
  ArbitraryTolerances = true
  EqualTolerance = false
  ExtensionAngle = 0
  FormatSpec = %.2w
  FormatSpecOverTolerance = +0
  FormatSpecUnderTolerance = -0.2
  Inverted = false
  LineAngle = 0
  LockPosition = false
  MeasureType = 1
  OverTolerance = 0
  References2D = -> [View]
  Rotation = 0
  ScaleType = 0
  TheoreticalExact = false
  Type = 2
  UnderTolerance = 0
  X = 63.1306
  Y = 3.23616
FEATURE [TechDraw::DrawComplexSection] ComplexSection  label="Section A - A"
  BaseView = -> View
  Caption = Section A-A
  CoarseView = false
  CutSurfaceDisplay = 2
  CuttingToolWireObject = -> Sketch026
  Direction = (0.0008,-1,-1e-06)
  FileGeomPattern = C:/Program Files/FreeCAD 0.21/data/Mod/TechDraw/PAT/FCPAT.pat
  FileHatchPattern = C:/Program Files/FreeCAD 0.21/data/Mod/TechDraw/Patterns/simple.svg
  Focus = 100
  FuseBeforeCut = false
  HardHidden = true
  HatchOffset = (0,0,0)
  HatchRotation = 0
  HatchScale = 1
  IsoCount = 0
  IsoHidden = false
  IsoVisible = true
  LockPosition = false
  NameGeomPattern = Gyémánt bevonatú
  Perspective = false
  ProjectionStrategy = 1
  Rotation = 0
  Scale = 10
  ScaleType = 2
  ScrubCount = 0
  SeamHidden = false
  SeamVisible = true
  SectionDirection = 4
  SectionNormal = (0.0008,-1,-1e-06)
  SectionOrigin = (0,0,0)
  SectionSymbol = A
  SmoothHidden = false
  SmoothVisible = true
  Source = -> [Body011]
  TrimAfterCut = false
  X = 271.86
  XDirection = (1,0.0008,8e-10)
  Y = 97.6511
FEATURE [TechDraw::DrawViewDimension] Dimension006
  AngleOverride = false
  Arbitrary = false
  ArbitraryTolerances = false
  EqualTolerance = true
  ExtensionAngle = 0
  FormatSpec = %.2w
  FormatSpecOverTolerance = %+.2w
  FormatSpecUnderTolerance = %+.2w
  Inverted = false
  LineAngle = 0
  LockPosition = false
  MeasureType = 1
  OverTolerance = 0
  References2D = -> [ComplexSection]
  Rotation = 0
  ScaleType = 0
  TheoreticalExact = false
  Type = 6
  UnderTolerance = 0
  X = -18.691
  Y = 25.4511
FEATURE [TechDraw::DrawViewDimension] Dimension007
  AngleOverride = false
  Arbitrary = false
  ArbitraryTolerances = false
  EqualTolerance = true
  ExtensionAngle = 0
  FormatSpec = 4× ⌀%.2w
  FormatSpecOverTolerance = %+.2w
  FormatSpecUnderTolerance = %+.2w
  Inverted = false
  LineAngle = 0
  LockPosition = false
  MeasureType = 1
  OverTolerance = 0
  References2D = -> [ComplexSection]
  Rotation = 0
  ScaleType = 0
  TheoreticalExact = false
  Type = 1
  UnderTolerance = 0
  X = 21.5378
  Y = 17.2051
FEATURE [TechDraw::DrawViewDimension] Dimension008
  AngleOverride = false
  Arbitrary = false
  ArbitraryTolerances = false
  EqualTolerance = true
  ExtensionAngle = 0
  FormatSpec = 4× ⌀%.2w
  FormatSpecOverTolerance = %+.2w
  FormatSpecUnderTolerance = %+.2w
  Inverted = false
  LineAngle = 0
  LockPosition = false
  MeasureType = 1
  OverTolerance = 0.05
  References2D = -> [ComplexSection]
  Rotation = 0
  ScaleType = 0
  TheoreticalExact = false
  Type = 1
  UnderTolerance = -0.05
  X = 55.092
  Y = -3.46373
FEATURE [TechDraw::DrawViewBalloon] Balloon003
  BubbleShape = 6
  EndType = 6
  EndTypeScale = 1
  KinkLength = 0
  LockPosition = false
  OriginX = 37.5325
  OriginY = -15.3767
  Rotation = 0
  ScaleType = 0
  ShapeScale = 1
  SourceView = -> Dimension008
  Text = ⌖|⌀0.15|A|B|C
  TextWrapLen = -1
  X = 66.8079
  Y = -14.5405
FEATURE [TechDraw::DrawViewBalloon] Balloon004
  BubbleShape = 6
  EndType = 6
  EndTypeScale = 1
  KinkLength = 0
  LockPosition = false
  OriginX = 71.9146
  OriginY = 52.1601
  Rotation = 0
  ScaleType = 0
  ShapeScale = 1
  SourceView = -> Dimension004
  Text = C
  TextWrapLen = -1
  X = 71.9416
  Y = 64.1709
FEATURE [TechDraw::DrawViewDimension] Dimension009
  AngleOverride = false
  Arbitrary = false
  ArbitraryTolerances = false
  EqualTolerance = true
  ExtensionAngle = 0
  FormatSpec = ⌀%.2w
  FormatSpecOverTolerance = %+.2w
  FormatSpecUnderTolerance = %+.2w
  Inverted = false
  LineAngle = 0
  LockPosition = false
  MeasureType = 1
  OverTolerance = 0
  References2D = -> [View]
  Rotation = 0
  ScaleType = 0
  TheoreticalExact = false
  Type = 1
  UnderTolerance = 0
  X = 41.6792
  Y = 87.8055
FEATURE [TechDraw::DrawViewBalloon] Balloon005
  BubbleShape = 6
  EndType = 6
  EndTypeScale = 1
  KinkLength = 0
  LockPosition = false
  OriginX = 40.9437
  OriginY = 76.3125
  Rotation = 0
  ScaleType = 0
  ShapeScale = 1
  SourceView = -> Dimension009
  Text = ⌖|⌀0.15|A|B|C
  TextWrapLen = -1
  X = 64.2909
  Y = 76.6252
FEATURE [TechDraw::DrawViewBalloon] Balloon006
  BubbleShape = 6
  EndType = 6
  EndTypeScale = 1
  KinkLength = -0.1
  LockPosition = false
  OriginX = 21.3573
  OriginY = 82.2819
  Rotation = 0
  ScaleType = 0
  ShapeScale = 1
  SourceView = -> Dimension009
  Text = D
  TextWrapLen = -1
  X = 11.5057
  Y = 82.2431
FEATURE [TechDraw::DrawViewDimension] Dimension010
  AngleOverride = false
  Arbitrary = false
  ArbitraryTolerances = false
  EqualTolerance = true
  ExtensionAngle = 0
  FormatSpec = (⌀%.2w)
  FormatSpecOverTolerance = %+.2w
  FormatSpecUnderTolerance = %+.2w
  Inverted = false
  LineAngle = 0
  LockPosition = false
  MeasureType = 1
  OverTolerance = 0
  References2D = -> [View005]
  Rotation = 0
  ScaleType = 0
  TheoreticalExact = false
  Type = 5
  UnderTolerance = 0
  X = -53.8815
  Y = 84.4487
FEATURE [TechDraw::DrawViewBalloon] Balloon007
  BubbleShape = 6
  EndType = 6
  EndTypeScale = 1
  KinkLength = 0
  LockPosition = false
  OriginX = -17.6685
  OriginY = 74.8861
  Rotation = 0
  ScaleType = 0
  ShapeScale = 1
  SourceView = -> Dimension010
  Text = ◎|⌀0.15|D
  TextWrapLen = -1
  X = -65.863
  Y = 73.3975
FEATURE [TechDraw::DrawViewDimension] Dimension011
  AngleOverride = false
  Arbitrary = false
  ArbitraryTolerances = false
  EqualTolerance = true
  ExtensionAngle = 0
  FormatSpec = 4× 2×R%.2w
  FormatSpecOverTolerance = %+.2w
  FormatSpecUnderTolerance = %+.2w
  Inverted = false
  LineAngle = 0
  LockPosition = false
  MeasureType = 1
  OverTolerance = 0
  References2D = -> [View005]
  Rotation = 0
  ScaleType = 0
  TheoreticalExact = false
  Type = 4
  UnderTolerance = 0
  X = 73.9281
  Y = -9.1821
FEATURE [TechDraw::DrawViewBalloon] Balloon008
  BubbleShape = 1
  EndType = 0
  EndTypeScale = 1
  KinkLength = 5
  LockPosition = false
  OriginX = 44.6662
  OriginY = 4.80573
  Rotation = 0
  ScaleType = 0
  ShapeScale = 1
  SourceView = -> View005
  Text = 4× 3×6
  TextWrapLen = -1
  X = 71.2925
  Y = -2.47903
FEATURE [TechDraw::DrawViewDimension] Dimension012
  AngleOverride = false
  Arbitrary = false
  ArbitraryTolerances = false
  EqualTolerance = true
  ExtensionAngle = 0
  FormatSpec = 5× ⌀%.2w
  FormatSpecOverTolerance = %+.2w
  FormatSpecUnderTolerance = %+.2w
  Inverted = false
  LineAngle = 0
  LockPosition = false
  MeasureType = 1
  OverTolerance = 0.05
  References2D = -> [View005]
  Rotation = 0
  ScaleType = 0
  TheoreticalExact = false
  Type = 5
  UnderTolerance = -0.05
  X = 6.26773
  Y = 86.6676
FEATURE [TechDraw::DrawViewBalloon] Balloon009
  BubbleShape = 6
  EndType = 6
  EndTypeScale = 1
  KinkLength = 0
  LockPosition = false
  OriginX = 1.847
  OriginY = 77.1251
  Rotation = 0
  ScaleType = 0
  ShapeScale = 1
  SourceView = -> Dimension012
  Text = ⌖|⌀0.15|A|B|C
  TextWrapLen = -1
  X = 20.2466
  Y = 75.5872
FEATURE [TechDraw::DrawViewDimension] Dimension013
  AngleOverride = false
  Arbitrary = false
  ArbitraryTolerances = true
  EqualTolerance = false
  ExtensionAngle = 0
  FormatSpec = %.2w
  FormatSpecOverTolerance = +0
  FormatSpecUnderTolerance = -0.2
  Inverted = false
  LineAngle = 0
  LockPosition = false
  MeasureType = 1
  OverTolerance = 0
  References2D = -> [View]
  Rotation = 0
  ScaleType = 0
  TheoreticalExact = false
  Type = 1
  UnderTolerance = 0
  X = -0.111347
  Y = -56.6908
FEATURE [TechDraw::DrawViewDimension] Dimension014
  AngleOverride = false
  Arbitrary = false
  ArbitraryTolerances = false
  EqualTolerance = true
  ExtensionAngle = 0
  FormatSpec = 8× %.2w
  FormatSpecOverTolerance = %+.2w
  FormatSpecUnderTolerance = %+.2w
  Inverted = false
  LineAngle = 0
  LockPosition = false
  MeasureType = 1
  OverTolerance = 0
  References2D = -> [View005]
  Rotation = 0
  ScaleType = 0
  TheoreticalExact = false
  Type = 1
  UnderTolerance = 0
  X = -40.1492
  Y = -56.125
FEATURE [TechDraw::DrawViewDimension] Dimension015
  AngleOverride = false
  Arbitrary = false
  ArbitraryTolerances = false
  EqualTolerance = true
  ExtensionAngle = 0
  FormatSpec = 8× %.2w
  FormatSpecOverTolerance = %+.2w
  FormatSpecUnderTolerance = %+.2w
  Inverted = false
  LineAngle = 0
  LockPosition = false
  MeasureType = 1
  OverTolerance = 0
  References2D = -> [View005]
  Rotation = 0
  ScaleType = 0
  TheoreticalExact = false
  Type = 2
  UnderTolerance = 0
  X = -59.7166
  Y = -36.8629
FEATURE [TechDraw::DrawViewDimension] Dimension016
  AngleOverride = false
  Arbitrary = false
  ArbitraryTolerances = false
  EqualTolerance = true
  ExtensionAngle = 0
  FormatSpec = 8× 4×R%.2w
  FormatSpecOverTolerance = %+.2w
  FormatSpecUnderTolerance = %+.2w
  Inverted = false
  LineAngle = 0
  LockPosition = false
  MeasureType = 1
  OverTolerance = 0
  References2D = -> [View005]
  Rotation = 0
  ScaleType = 0
  TheoreticalExact = false
  Type = 4
  UnderTolerance = 0
  X = -71.0294
  Y = -13.1757
FEATURE [TechDraw::DrawViewBalloon] Balloon010
  BubbleShape = 6
  EndType = 0
  EndTypeScale = 1
  KinkLength = 5
  LockPosition = false
  OriginX = -5.56188
  OriginY = -47.7444
  Rotation = 0
  ScaleType = 0
  ShapeScale = 1
  SourceView = -> View005
  Text = ⌓|0.2|A|B|C
  TextWrapLen = -1
  X = 36.7846
  Y = -75.6976
FEATURE [TechDraw::DrawViewAnnotation] Annotation
  Font = osifont
  LineSpace = 100
  LockPosition = false
  MaxWidth = -1
  Rotation = 0
  ScaleType = 0
  Text = 8x
  TextSize = 4
  TextStyle = 0
  X = 333.557
  Y = 130.718
FEATURE [TechDraw::DrawViewAnnotation] Annotation001
  Font = osifont
  LineSpace = 100
  LockPosition = false
  MaxWidth = -1
  Rotation = 0
  ScaleType = 0
  Text = 10:1
  TextSize = 4
  TextStyle = 0
  X = 268.793
  Y = 76.5553
FEATURE [TechDraw::DrawViewAnnotation] Annotation002
  Font = osifont
  LineSpace = 100
  LockPosition = false
  MaxWidth = -1
  Rotation = 0
  ScaleType = 0
  Text = The mid of the datum plane A is preferred to be near | to the lower limit of the flatness tolerance zone. | It can be achieved with an additional bending step. | Aesthetical surfaces colored red on the view | No scratches, burrs or any kind of damage allowed! | Functional surfaces colored blue on the view (all which perpendicular to the aesthetical) | No burrs or other protruding material allowed!
  TextSize = 3
  TextStyle = 0
  X = 95.1612
  Y = 45.9572
FEATURE [TechDraw::DrawViewBalloon] Balloon011
  BubbleShape = 1
  EndType = 3
  EndTypeScale = 1
  KinkLength = 0
  LockPosition = false
  OriginX = -0.4647
  OriginY = -15.1475
  Rotation = 0
  ScaleType = 0
  ShapeScale = 1
  SourceView = -> View007
  TextWrapLen = -1
  X = -116.572
  Y = -67.6818
FEATURE [TechDraw::DrawHatch] Hatch001  label="Hatch001F20"
  HatchPattern = C:/Program Files/FreeCAD 0.21/data/Mod/TechDraw/Patterns/solid.svg
  Source = -> View007 [Face20,Face60,Face113,Face21,Face63,Face74,Face73,Face75,Face76,Face72,Face111,Face24,Face83,Face80,Face119,Face77,Face25,Face112,Face30,Face61,Face71,Face35,Face42,Face97,Face105,Face40,Face69,Face41,Face96,Face67,Face33,Face104,Face37,Face101,Face68,Face39,Face102,Face31,Face109,Face108,+30 more]
FEATURE [TechDraw::DrawViewBalloon] Balloon012
  BubbleShape = 6
  EndType = 6
  EndTypeScale = 1
  KinkLength = 0
  LockPosition = false
  OriginX = 52.0739
  OriginY = -63.6754
  Rotation = 0
  ScaleType = 0
  ShapeScale = 1
  SourceView = -> Dimension013
  Text = B
  TextWrapLen = -1
  X = 63.1195
  Y = -63.7162
FEATURE [TechDraw::DrawViewAnnotation] Annotation003
  Font = osifont
  LineSpace = 100
  LockPosition = false
  MaxWidth = -1
  Rotation = 0
  ScaleType = 0
  Text = 1:2
  TextSize = 4
  TextStyle = 0
  X = 173.589
  Y = 48.2528
FEATURE [TechDraw::DrawPage] Page  label="VSN1_Drawing"
  KeepUpdated = true
  NextBalloonIndex = 15
  ProjectionType = 0
  Template = -> Template
  Views = -> [View,View005,View006,View007,Dimension001,Dimension002,Balloon,Dimension,Dimension003,Balloon001,Balloon002,Dimension004,ComplexSection,Dimension006,Dimension007,Dimension008,Balloon003,Balloon004,Dimension009,Balloon005,Balloon006,Dimension010,Balloon007,Dimension011,Balloon008,Dimension012,Balloon009,Dimension013,Dimension014,Dimension015,Dimension016,Balloon010,Annotation,Annotation001,+4 more]
FEATURE [TechDraw::DrawHatch] Hatch002  label="Hatch002F12"
  HatchPattern = C:/Program Files/FreeCAD 0.21/data/Mod/TechDraw/Patterns/solid.svg
  Source = -> View007 [Face12,Face18,Face17,Face13,Face14,Face15,Face16]
FEATURE [TechDraw::DrawHatch] Hatch003  label="Hatch003F19"
  HatchPattern = C:/Program Files/FreeCAD 0.21/data/Mod/TechDraw/Patterns/solid.svg
  Source = -> View007 [Face19,Face3,Face23]
FEATURE [TechDraw::DrawHatch] Hatch004  label="Hatch004F1"
  HatchPattern = C:/Program Files/FreeCAD 0.21/data/Mod/TechDraw/Patterns/simple.svg
  Source = -> ComplexSection [Face1,Face2]
